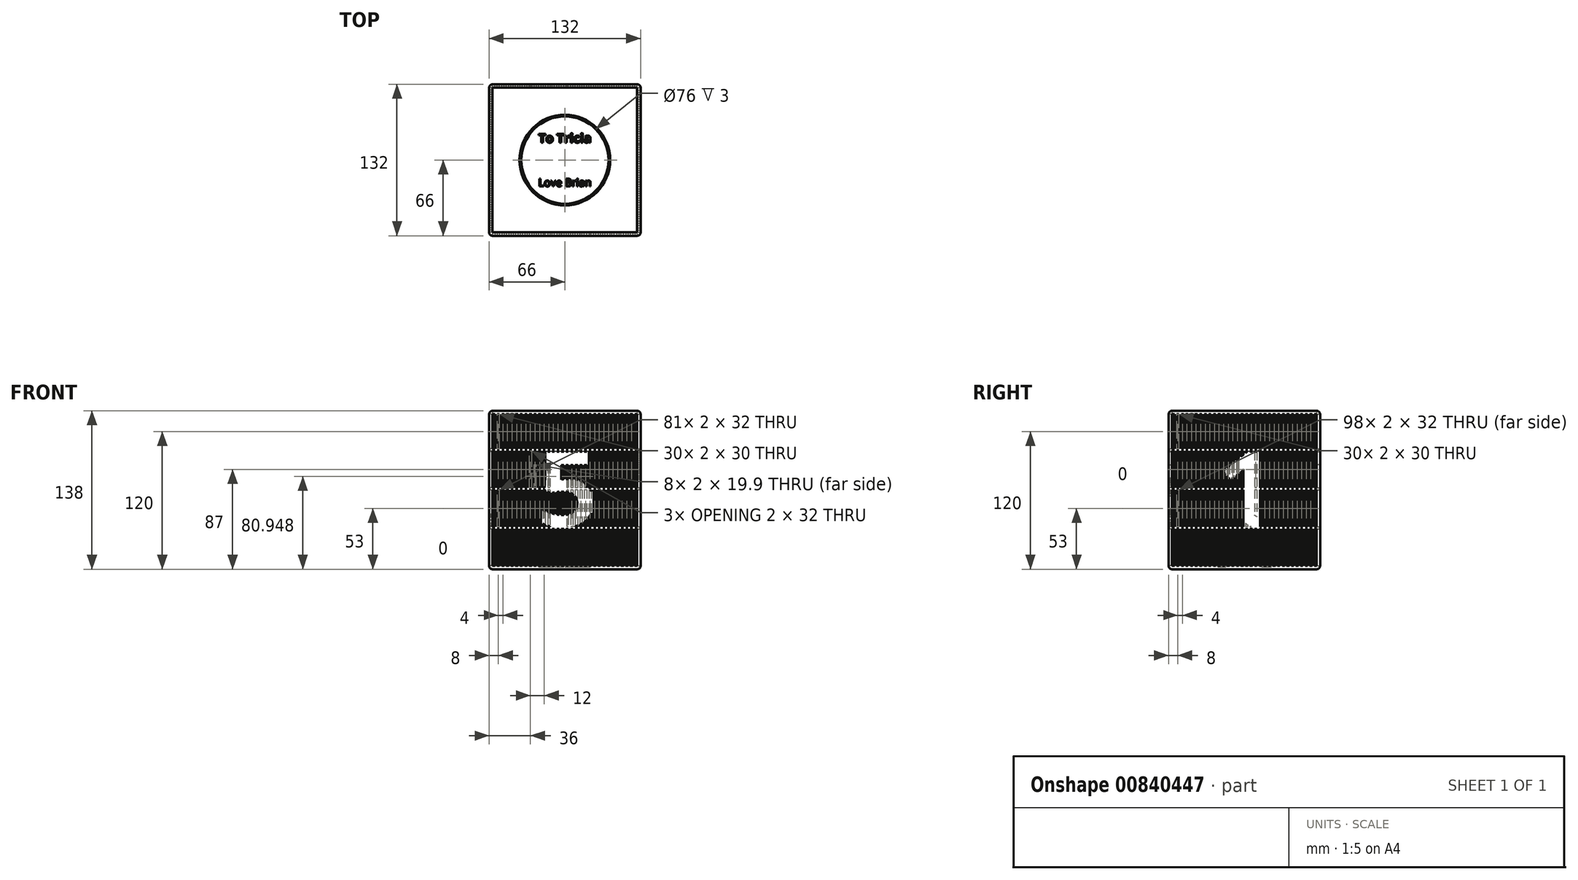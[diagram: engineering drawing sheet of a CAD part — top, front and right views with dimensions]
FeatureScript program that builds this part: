
annotation { "Feature Type Name" : "Feature", "Feature Type Description" : "" }
export const myFeature = defineFeature(function(context is Context, id is Id, definition is map)
    precondition{}
    {
        {
            var Q0;
            Q0=qCreatedBy(makeId("Top.planeOp"),FACE);
            var sketch = newSketch(context, id + "F0", { "sketchPlane" : qUnion([Q0])});
            skLineSegment(sketch, "E0.bottom", {"start": v(-66, 66) * mm, "end": v(66, 66) * mm});
            skLineSegment(sketch, "E0.top", {"start": v(-66, -66) * mm, "end": v(66, -66) * mm});
            skLineSegment(sketch, "E0.left", {"start": v(-66, 66) * mm, "end": v(-66, -66) * mm});
            skLineSegment(sketch, "E0.right", {"start": v(66, 66) * mm, "end": v(66, -66) * mm});
            skPoint(sketch, "E0.middle", {"position": v(0, 0) * mm});
            skSolve(sketch);
        }
        {
            var Q0;
            Q0 = qSketchRegion(id + "F0", true);
            extrude(context, id + "F1", {"entities" : qUnion([Q0]), "depth" : 3 * mm, "offsetDistance" : 25 * mm});
        }
        {
            var Q0;
            Q0=makeQuery(id+"F1.opExtrude","CAP_FACE",FACE,{"disambiguationData":[OSD([sQuery(id+"F0.wireOp",EDGE,"E0.bottom"),sQuery(id+"F0.wireOp",EDGE,"E0.top"),sQuery(id+"F0.wireOp",EDGE,"E0.left"),sQuery(id+"F0.wireOp",EDGE,"E0.right")])],"isStart":false});
            var sketch = newSketch(context, id + "F2", { "sketchPlane" : qUnion([Q0])});
            skCircle(sketch, "E1", {"center": v(0, 0) * mm, "radius": 38 * mm});
            skCircle(sketch, "E2", {"center": v(0, 0) * mm, "radius": 39.5 * mm});
            skSolve(sketch);
        }
        {
            var Q0;
            Q0 = qSketchRegion(id + "F2", true);
            extrude(context, id + "F3", {"entities" : qUnion([Q0]), "operationType" : NewBodyOperationType.ADD, "depth" : 3 * mm, "offsetDistance" : 25 * mm});
        }
        {
            var Q0;
            {var subQ0=sQuery(id+"F0.wireOp",EDGE,"E0.left");var subQ1=sQuery(id+"F0.wireOp",EDGE,"E0.top");var subQ2=sQuery(id+"F0.wireOp",EDGE,"E0.right");var subQ3=sQuery(id+"F0.wireOp",EDGE,"E0.bottom");Q0=makeQuery(id+"F3.boolean.opBoolean","SPLIT",FACE,{"disambiguationData":[TD([makeQuery(id+"F1.opExtrude","SWEPT_FACE",FACE,{"disambiguationData":[OSD([subQ3])]})])],"derivedFrom":makeQuery(id+"F1.opExtrude","CAP_FACE",FACE,{"disambiguationData":[OSD([subQ3,subQ1,subQ0,subQ2])],"isStart":false})});}
            var sketch = newSketch(context, id + "F4", { "sketchPlane" : qUnion([Q0])});
            skLineSegment(sketch, "E3.bottom", {"start": v(-66, 66) * mm, "end": v(66, 66) * mm});
            skLineSegment(sketch, "E3.top", {"start": v(-66, -66) * mm, "end": v(66, -66) * mm});
            skLineSegment(sketch, "E3.left", {"start": v(-66, 66) * mm, "end": v(-66, -66) * mm});
            skLineSegment(sketch, "E3.right", {"start": v(66, 66) * mm, "end": v(66, -66) * mm});
            skPoint(sketch, "E3.middle", {"position": v(0, 0) * mm});
            skLineSegment(sketch, "E4.bottom", {"start": v(-63, 63) * mm, "end": v(63, 63) * mm});
            skLineSegment(sketch, "E4.top", {"start": v(-63, -63) * mm, "end": v(63, -63) * mm});
            skLineSegment(sketch, "E4.left", {"start": v(-63, 63) * mm, "end": v(-63, -63) * mm});
            skLineSegment(sketch, "E4.right", {"start": v(63, 63) * mm, "end": v(63, -63) * mm});
            skSolve(sketch);
        }
        {
            var Q0;
            Q0 = qSketchRegion(id + "F4", true);
            extrude(context, id + "F5", {"entities" : qUnion([Q0]), "operationType" : NewBodyOperationType.ADD, "depth" : 135 * mm, "offsetDistance" : 25 * mm});
        }
        {
            var Q0;
            Q0=makeQuery(id+"F5.opExtrude","CAP_EDGE",EDGE,{"disambiguationData":[OSD([sQuery(id+"F4.wireOp",EDGE,"E3.bottom")])],"isStart":false});
            var Q1;
            Q1=makeQuery(id+"F5.opExtrude","CAP_EDGE",EDGE,{"disambiguationData":[OSD([sQuery(id+"F4.wireOp",EDGE,"E3.left")])],"isStart":false});
            var Q2;
            Q2=makeQuery(id+"F5.opExtrude","CAP_EDGE",EDGE,{"disambiguationData":[OSD([sQuery(id+"F4.wireOp",EDGE,"E3.top")])],"isStart":false});
            var Q3;
            Q3=makeQuery(id+"F5.opExtrude","CAP_EDGE",EDGE,{"disambiguationData":[OSD([sQuery(id+"F4.wireOp",EDGE,"E3.right")])],"isStart":false});
            var Q4;
            Q4=makeQuery(id+"F5.boolean.opBoolean","MERGE",EDGE,{"derivedFrom":[makeQuery(id+"F1.opExtrude","SWEPT_EDGE",EDGE,{"disambiguationData":[OSD([sQuery(id+"F0.wireOp",EDGE,"E0.top"),sQuery(id+"F0.wireOp",EDGE,"E0.right")])]}),makeQuery(id+"F5.opExtrude","SWEPT_EDGE",EDGE,{"disambiguationData":[OSD([sQuery(id+"F4.wireOp",EDGE,"E3.top"),sQuery(id+"F4.wireOp",EDGE,"E3.right")])]})]});
            var Q5;
            Q5=makeQuery(id+"F5.boolean.opBoolean","MERGE",EDGE,{"derivedFrom":[makeQuery(id+"F1.opExtrude","SWEPT_EDGE",EDGE,{"disambiguationData":[OSD([sQuery(id+"F0.wireOp",EDGE,"E0.top"),sQuery(id+"F0.wireOp",EDGE,"E0.left")])]}),makeQuery(id+"F5.opExtrude","SWEPT_EDGE",EDGE,{"disambiguationData":[OSD([sQuery(id+"F4.wireOp",EDGE,"E3.top"),sQuery(id+"F4.wireOp",EDGE,"E3.left")])]})]});
            var Q6;
            Q6=makeQuery(id+"F5.boolean.opBoolean","MERGE",EDGE,{"derivedFrom":[makeQuery(id+"F1.opExtrude","SWEPT_EDGE",EDGE,{"disambiguationData":[OSD([sQuery(id+"F0.wireOp",EDGE,"E0.bottom"),sQuery(id+"F0.wireOp",EDGE,"E0.left")])]}),makeQuery(id+"F5.opExtrude","SWEPT_EDGE",EDGE,{"disambiguationData":[OSD([sQuery(id+"F4.wireOp",EDGE,"E3.bottom"),sQuery(id+"F4.wireOp",EDGE,"E3.left")])]})]});
            var Q7;
            Q7=makeQuery(id+"F5.boolean.opBoolean","MERGE",EDGE,{"derivedFrom":[makeQuery(id+"F1.opExtrude","SWEPT_EDGE",EDGE,{"disambiguationData":[OSD([sQuery(id+"F0.wireOp",EDGE,"E0.bottom"),sQuery(id+"F0.wireOp",EDGE,"E0.right")])]}),makeQuery(id+"F5.opExtrude","SWEPT_EDGE",EDGE,{"disambiguationData":[OSD([sQuery(id+"F4.wireOp",EDGE,"E3.bottom"),sQuery(id+"F4.wireOp",EDGE,"E3.right")])]})]});
            var Q8;
            Q8=makeQuery(id+"F1.opExtrude","CAP_EDGE",EDGE,{"disambiguationData":[OSD([sQuery(id+"F0.wireOp",EDGE,"E0.bottom")])],"isStart":true});
            var Q9;
            Q9=makeQuery(id+"F1.opExtrude","CAP_EDGE",EDGE,{"disambiguationData":[OSD([sQuery(id+"F0.wireOp",EDGE,"E0.right")])],"isStart":true});
            var Q10;
            Q10=makeQuery(id+"F1.opExtrude","CAP_EDGE",EDGE,{"disambiguationData":[OSD([sQuery(id+"F0.wireOp",EDGE,"E0.left")])],"isStart":true});
            var Q11;
            Q11=makeQuery(id+"F1.opExtrude","CAP_EDGE",EDGE,{"disambiguationData":[OSD([sQuery(id+"F0.wireOp",EDGE,"E0.top")])],"isStart":true});
            fillet(context, id + "F6", {"entities" : qUnion([Q0, Q1, Q2, Q3, Q4, Q5, Q6, Q7, Q8, Q9, Q10, Q11]), "radius" : 3 * mm, "tangentPropagation" : true, "allowEdgeOverflow" : false});
        }
        {
            var Q0;
            Q0=makeQuery(id+"F5.boolean.opBoolean","MERGE",FACE,{"derivedFrom":[makeQuery(id+"F1.opExtrude","SWEPT_FACE",FACE,{"disambiguationData":[OSD([sQuery(id+"F0.wireOp",EDGE,"E0.top")])]}),makeQuery(id+"F5.opExtrude","SWEPT_FACE",FACE,{"disambiguationData":[OSD([sQuery(id+"F4.wireOp",EDGE,"E3.top")])]})]});
            var sketch = newSketch(context, id + "F7", { "sketchPlane" : qUnion([Q0])});
            skLineSegment(sketch, "E5.bottom", {"start": v(-63, 135) * mm, "end": v(-61, 135) * mm});
            skLineSegment(sketch, "E5.top", {"start": v(-63, 3) * mm, "end": v(-61, 3) * mm});
            skLineSegment(sketch, "E5.left", {"start": v(-63, 135) * mm, "end": v(-63, 3) * mm});
            skLineSegment(sketch, "E5.right", {"start": v(-61, 135) * mm, "end": v(-61, 3) * mm});
            skLineSegment(sketch, "E6.bottom", {"start": v(-59, 135) * mm, "end": v(-57, 135) * mm});
            skLineSegment(sketch, "E6.top", {"start": v(-59, 3) * mm, "end": v(-57, 3) * mm});
            skLineSegment(sketch, "E6.left", {"start": v(-59, 135) * mm, "end": v(-59, 3) * mm});
            skLineSegment(sketch, "E6.right", {"start": v(-57, 135) * mm, "end": v(-57, 3) * mm});
            skLineSegment(sketch, "E7.bottom", {"start": v(-55, 135) * mm, "end": v(-53, 135) * mm});
            skLineSegment(sketch, "E7.top", {"start": v(-55, 3) * mm, "end": v(-53, 3) * mm});
            skLineSegment(sketch, "E7.left", {"start": v(-55, 135) * mm, "end": v(-55, 3) * mm});
            skLineSegment(sketch, "E7.right", {"start": v(-53, 135) * mm, "end": v(-53, 3) * mm});
            skLineSegment(sketch, "E8.bottom", {"start": v(-51, 135) * mm, "end": v(-49, 135) * mm});
            skLineSegment(sketch, "E8.top", {"start": v(-51, 3) * mm, "end": v(-49, 3) * mm});
            skLineSegment(sketch, "E8.left", {"start": v(-51, 135) * mm, "end": v(-51, 3) * mm});
            skLineSegment(sketch, "E8.right", {"start": v(-49, 135) * mm, "end": v(-49, 3) * mm});
            skLineSegment(sketch, "E9.bottom", {"start": v(-47, 135) * mm, "end": v(-45, 135) * mm});
            skLineSegment(sketch, "E9.top", {"start": v(-47, 3) * mm, "end": v(-45, 3) * mm});
            skLineSegment(sketch, "E9.left", {"start": v(-47, 135) * mm, "end": v(-47, 3) * mm});
            skLineSegment(sketch, "E9.right", {"start": v(-45, 135) * mm, "end": v(-45, 3) * mm});
            skLineSegment(sketch, "E10.bottom", {"start": v(-43, 135) * mm, "end": v(-41, 135) * mm});
            skLineSegment(sketch, "E10.top", {"start": v(-43, 3) * mm, "end": v(-41, 3) * mm});
            skLineSegment(sketch, "E10.left", {"start": v(-43, 135) * mm, "end": v(-43, 3) * mm});
            skLineSegment(sketch, "E10.right", {"start": v(-41, 135) * mm, "end": v(-41, 3) * mm});
            skLineSegment(sketch, "E11.bottom", {"start": v(-39, 135) * mm, "end": v(-37, 135) * mm});
            skLineSegment(sketch, "E11.top", {"start": v(-39, 3) * mm, "end": v(-37, 3) * mm});
            skLineSegment(sketch, "E11.left", {"start": v(-39, 135) * mm, "end": v(-39, 3) * mm});
            skLineSegment(sketch, "E11.right", {"start": v(-37, 135) * mm, "end": v(-37, 3) * mm});
            skLineSegment(sketch, "E12.bottom", {"start": v(-35, 135) * mm, "end": v(-33, 135) * mm});
            skLineSegment(sketch, "E12.top", {"start": v(-35, 3) * mm, "end": v(-33, 3) * mm});
            skLineSegment(sketch, "E12.left", {"start": v(-35, 135) * mm, "end": v(-35, 3) * mm});
            skLineSegment(sketch, "E12.right", {"start": v(-33, 135) * mm, "end": v(-33, 3) * mm});
            skLineSegment(sketch, "E13.bottom", {"start": v(-31, 135) * mm, "end": v(-29, 135) * mm});
            skLineSegment(sketch, "E13.top", {"start": v(-31, 3) * mm, "end": v(-29, 3) * mm});
            skLineSegment(sketch, "E13.left", {"start": v(-31, 135) * mm, "end": v(-31, 3) * mm});
            skLineSegment(sketch, "E13.right", {"start": v(-29, 135) * mm, "end": v(-29, 3) * mm});
            skLineSegment(sketch, "E14.bottom", {"start": v(-27, 135) * mm, "end": v(-25, 135) * mm});
            skLineSegment(sketch, "E14.top", {"start": v(-27, 3) * mm, "end": v(-25, 3) * mm});
            skLineSegment(sketch, "E14.left", {"start": v(-27, 135) * mm, "end": v(-27, 3) * mm});
            skLineSegment(sketch, "E14.right", {"start": v(-25, 135) * mm, "end": v(-25, 3) * mm});
            skLineSegment(sketch, "E15.bottom", {"start": v(-23, 135) * mm, "end": v(-21, 135) * mm});
            skLineSegment(sketch, "E15.top", {"start": v(-23, 3) * mm, "end": v(-21, 3) * mm});
            skLineSegment(sketch, "E15.left", {"start": v(-23, 135) * mm, "end": v(-23, 3) * mm});
            skLineSegment(sketch, "E15.right", {"start": v(-21, 135) * mm, "end": v(-21, 3) * mm});
            skLineSegment(sketch, "E16.bottom", {"start": v(-19, 3) * mm, "end": v(-17, 3) * mm});
            skLineSegment(sketch, "E16.top", {"start": v(-19, 135) * mm, "end": v(-17, 135) * mm});
            skLineSegment(sketch, "E16.left", {"start": v(-19, 3) * mm, "end": v(-19, 135) * mm});
            skLineSegment(sketch, "E16.right", {"start": v(-17, 3) * mm, "end": v(-17, 135) * mm});
            skLineSegment(sketch, "E17.bottom", {"start": v(-15, 135) * mm, "end": v(-13, 135) * mm});
            skLineSegment(sketch, "E17.top", {"start": v(-15, 3) * mm, "end": v(-13, 3) * mm});
            skLineSegment(sketch, "E17.left", {"start": v(-15, 135) * mm, "end": v(-15, 3) * mm});
            skLineSegment(sketch, "E17.right", {"start": v(-13, 135) * mm, "end": v(-13, 3) * mm});
            skLineSegment(sketch, "E18.bottom", {"start": v(-11, 3) * mm, "end": v(-9, 3) * mm});
            skLineSegment(sketch, "E18.top", {"start": v(-11, 135) * mm, "end": v(-9, 135) * mm});
            skLineSegment(sketch, "E18.left", {"start": v(-11, 3) * mm, "end": v(-11, 135) * mm});
            skLineSegment(sketch, "E18.right", {"start": v(-9, 3) * mm, "end": v(-9, 135) * mm});
            skLineSegment(sketch, "E19.bottom", {"start": v(-7, 135) * mm, "end": v(-5, 135) * mm});
            skLineSegment(sketch, "E19.top", {"start": v(-7, 3) * mm, "end": v(-5, 3) * mm});
            skLineSegment(sketch, "E19.left", {"start": v(-7, 135) * mm, "end": v(-7, 3) * mm});
            skLineSegment(sketch, "E19.right", {"start": v(-5, 135) * mm, "end": v(-5, 3) * mm});
            skLineSegment(sketch, "E20.bottom", {"start": v(-3, 3) * mm, "end": v(-1, 3) * mm});
            skLineSegment(sketch, "E20.top", {"start": v(-3, 135) * mm, "end": v(-1, 135) * mm});
            skLineSegment(sketch, "E20.left", {"start": v(-3, 3) * mm, "end": v(-3, 135) * mm});
            skLineSegment(sketch, "E20.right", {"start": v(-1, 3) * mm, "end": v(-1, 135) * mm});
            skLineSegment(sketch, "E21.bottom", {"start": v(1, 135) * mm, "end": v(3, 135) * mm});
            skLineSegment(sketch, "E21.top", {"start": v(1, 3) * mm, "end": v(3, 3) * mm});
            skLineSegment(sketch, "E21.left", {"start": v(1, 135) * mm, "end": v(1, 3) * mm});
            skLineSegment(sketch, "E21.right", {"start": v(3, 135) * mm, "end": v(3, 3) * mm});
            skLineSegment(sketch, "E22.bottom", {"start": v(5, 3) * mm, "end": v(7, 3) * mm});
            skLineSegment(sketch, "E22.top", {"start": v(5, 135) * mm, "end": v(7, 135) * mm});
            skLineSegment(sketch, "E22.left", {"start": v(5, 3) * mm, "end": v(5, 135) * mm});
            skLineSegment(sketch, "E22.right", {"start": v(7, 3) * mm, "end": v(7, 135) * mm});
            skLineSegment(sketch, "E23.bottom", {"start": v(9, 135) * mm, "end": v(11, 135) * mm});
            skLineSegment(sketch, "E23.top", {"start": v(9, 3) * mm, "end": v(11, 3) * mm});
            skLineSegment(sketch, "E23.left", {"start": v(9, 135) * mm, "end": v(9, 3) * mm});
            skLineSegment(sketch, "E23.right", {"start": v(11, 135) * mm, "end": v(11, 3) * mm});
            skLineSegment(sketch, "E24.bottom", {"start": v(13, 3) * mm, "end": v(15, 3) * mm});
            skLineSegment(sketch, "E24.top", {"start": v(13, 135) * mm, "end": v(15, 135) * mm});
            skLineSegment(sketch, "E24.left", {"start": v(13, 3) * mm, "end": v(13, 135) * mm});
            skLineSegment(sketch, "E24.right", {"start": v(15, 3) * mm, "end": v(15, 135) * mm});
            skLineSegment(sketch, "E25.bottom", {"start": v(17, 135) * mm, "end": v(19, 135) * mm});
            skLineSegment(sketch, "E25.top", {"start": v(17, 3) * mm, "end": v(19, 3) * mm});
            skLineSegment(sketch, "E25.left", {"start": v(17, 135) * mm, "end": v(17, 3) * mm});
            skLineSegment(sketch, "E25.right", {"start": v(19, 135) * mm, "end": v(19, 3) * mm});
            skLineSegment(sketch, "E26.bottom", {"start": v(21, 135) * mm, "end": v(23, 135) * mm});
            skLineSegment(sketch, "E26.top", {"start": v(21, 3) * mm, "end": v(23, 3) * mm});
            skLineSegment(sketch, "E26.left", {"start": v(21, 135) * mm, "end": v(21, 3) * mm});
            skLineSegment(sketch, "E26.right", {"start": v(23, 135) * mm, "end": v(23, 3) * mm});
            skLineSegment(sketch, "E27.bottom", {"start": v(25, 3) * mm, "end": v(27, 3) * mm});
            skLineSegment(sketch, "E27.top", {"start": v(25, 135) * mm, "end": v(27, 135) * mm});
            skLineSegment(sketch, "E27.left", {"start": v(25, 3) * mm, "end": v(25, 135) * mm});
            skLineSegment(sketch, "E27.right", {"start": v(27, 3) * mm, "end": v(27, 135) * mm});
            skLineSegment(sketch, "E28.bottom", {"start": v(29, 135) * mm, "end": v(31, 135) * mm});
            skLineSegment(sketch, "E28.top", {"start": v(29, 3) * mm, "end": v(31, 3) * mm});
            skLineSegment(sketch, "E28.left", {"start": v(29, 135) * mm, "end": v(29, 3) * mm});
            skLineSegment(sketch, "E28.right", {"start": v(31, 135) * mm, "end": v(31, 3) * mm});
            skLineSegment(sketch, "E29.bottom", {"start": v(33, 3) * mm, "end": v(35, 3) * mm});
            skLineSegment(sketch, "E29.top", {"start": v(33, 135) * mm, "end": v(35, 135) * mm});
            skLineSegment(sketch, "E29.left", {"start": v(33, 3) * mm, "end": v(33, 135) * mm});
            skLineSegment(sketch, "E29.right", {"start": v(35, 3) * mm, "end": v(35, 135) * mm});
            skLineSegment(sketch, "E30.bottom", {"start": v(37, 135) * mm, "end": v(39, 135) * mm});
            skLineSegment(sketch, "E30.top", {"start": v(37, 3) * mm, "end": v(39, 3) * mm});
            skLineSegment(sketch, "E30.left", {"start": v(37, 135) * mm, "end": v(37, 3) * mm});
            skLineSegment(sketch, "E30.right", {"start": v(39, 135) * mm, "end": v(39, 3) * mm});
            skLineSegment(sketch, "E31.bottom", {"start": v(41, 3) * mm, "end": v(43, 3) * mm});
            skLineSegment(sketch, "E31.top", {"start": v(41, 135) * mm, "end": v(43, 135) * mm});
            skLineSegment(sketch, "E31.left", {"start": v(41, 3) * mm, "end": v(41, 135) * mm});
            skLineSegment(sketch, "E31.right", {"start": v(43, 3) * mm, "end": v(43, 135) * mm});
            skLineSegment(sketch, "E32.bottom", {"start": v(45, 135) * mm, "end": v(47, 135) * mm});
            skLineSegment(sketch, "E32.top", {"start": v(45, 3) * mm, "end": v(47, 3) * mm});
            skLineSegment(sketch, "E32.left", {"start": v(45, 135) * mm, "end": v(45, 3) * mm});
            skLineSegment(sketch, "E32.right", {"start": v(47, 135) * mm, "end": v(47, 3) * mm});
            skLineSegment(sketch, "E33.bottom", {"start": v(49, 3) * mm, "end": v(51, 3) * mm});
            skLineSegment(sketch, "E33.top", {"start": v(49, 135) * mm, "end": v(51, 135) * mm});
            skLineSegment(sketch, "E33.left", {"start": v(49, 3) * mm, "end": v(49, 135) * mm});
            skLineSegment(sketch, "E33.right", {"start": v(51, 3) * mm, "end": v(51, 135) * mm});
            skLineSegment(sketch, "E34.bottom", {"start": v(53, 135) * mm, "end": v(55, 135) * mm});
            skLineSegment(sketch, "E34.top", {"start": v(53, 3) * mm, "end": v(55, 3) * mm});
            skLineSegment(sketch, "E34.left", {"start": v(53, 135) * mm, "end": v(53, 3) * mm});
            skLineSegment(sketch, "E34.right", {"start": v(55, 135) * mm, "end": v(55, 3) * mm});
            skLineSegment(sketch, "E35.bottom", {"start": v(57, 135) * mm, "end": v(59, 135) * mm});
            skLineSegment(sketch, "E35.top", {"start": v(57, 3) * mm, "end": v(59, 3) * mm});
            skLineSegment(sketch, "E35.left", {"start": v(57, 135) * mm, "end": v(57, 3) * mm});
            skLineSegment(sketch, "E35.right", {"start": v(59, 135) * mm, "end": v(59, 3) * mm});
            skLineSegment(sketch, "E36.bottom", {"start": v(61, 135) * mm, "end": v(63, 135) * mm});
            skLineSegment(sketch, "E36.top", {"start": v(61, 3) * mm, "end": v(63, 3) * mm});
            skLineSegment(sketch, "E36.left", {"start": v(61, 135) * mm, "end": v(61, 3) * mm});
            skLineSegment(sketch, "E36.right", {"start": v(63, 135) * mm, "end": v(63, 3) * mm});
            skSolve(sketch);
        }
        {
            var Q0;
            Q0 = qSketchRegion(id + "F7", true);
            extrude(context, id + "F8", {"entities" : qUnion([Q0]), "operationType" : NewBodyOperationType.REMOVE, "oppositeDirection" : true, "depth" : 3 * mm, "offsetDistance" : 25 * mm});
        }
        {
            var Q0;
            Q0=makeQuery(id+"F5.boolean.opBoolean","MERGE",FACE,{"derivedFrom":[makeQuery(id+"F1.opExtrude","SWEPT_FACE",FACE,{"disambiguationData":[OSD([sQuery(id+"F0.wireOp",EDGE,"E0.right")])]}),makeQuery(id+"F5.opExtrude","SWEPT_FACE",FACE,{"disambiguationData":[OSD([sQuery(id+"F4.wireOp",EDGE,"E3.right")])]})]});
            var sketch = newSketch(context, id + "F9", { "sketchPlane" : qUnion([Q0])});
            skLineSegment(sketch, "E37.bottom", {"start": v(-63, 135) * mm, "end": v(-61, 135) * mm});
            skLineSegment(sketch, "E37.top", {"start": v(-63, 3) * mm, "end": v(-61, 3) * mm});
            skLineSegment(sketch, "E37.left", {"start": v(-63, 135) * mm, "end": v(-63, 3) * mm});
            skLineSegment(sketch, "E37.right", {"start": v(-61, 135) * mm, "end": v(-61, 3) * mm});
            skLineSegment(sketch, "E38.bottom", {"start": v(-59, 135) * mm, "end": v(-57, 135) * mm});
            skLineSegment(sketch, "E38.top", {"start": v(-59, 3) * mm, "end": v(-57, 3) * mm});
            skLineSegment(sketch, "E38.left", {"start": v(-59, 135) * mm, "end": v(-59, 3) * mm});
            skLineSegment(sketch, "E38.right", {"start": v(-57, 135) * mm, "end": v(-57, 3) * mm});
            skLineSegment(sketch, "E39.bottom", {"start": v(-55, 135) * mm, "end": v(-53, 135) * mm});
            skLineSegment(sketch, "E39.top", {"start": v(-55, 3) * mm, "end": v(-53, 3) * mm});
            skLineSegment(sketch, "E39.left", {"start": v(-55, 135) * mm, "end": v(-55, 3) * mm});
            skLineSegment(sketch, "E39.right", {"start": v(-53, 135) * mm, "end": v(-53, 3) * mm});
            skLineSegment(sketch, "E40.bottom", {"start": v(-51, 135) * mm, "end": v(-49, 135) * mm});
            skLineSegment(sketch, "E40.top", {"start": v(-51, 3) * mm, "end": v(-49, 3) * mm});
            skLineSegment(sketch, "E40.left", {"start": v(-51, 135) * mm, "end": v(-51, 3) * mm});
            skLineSegment(sketch, "E40.right", {"start": v(-49, 135) * mm, "end": v(-49, 3) * mm});
            skLineSegment(sketch, "E41.bottom", {"start": v(-47, 135) * mm, "end": v(-45, 135) * mm});
            skLineSegment(sketch, "E41.top", {"start": v(-47, 3) * mm, "end": v(-45, 3) * mm});
            skLineSegment(sketch, "E41.left", {"start": v(-47, 135) * mm, "end": v(-47, 3) * mm});
            skLineSegment(sketch, "E41.right", {"start": v(-45, 135) * mm, "end": v(-45, 3) * mm});
            skLineSegment(sketch, "E42.bottom", {"start": v(-43, 135) * mm, "end": v(-41, 135) * mm});
            skLineSegment(sketch, "E42.top", {"start": v(-43, 3) * mm, "end": v(-41, 3) * mm});
            skLineSegment(sketch, "E42.left", {"start": v(-43, 135) * mm, "end": v(-43, 3) * mm});
            skLineSegment(sketch, "E42.right", {"start": v(-41, 135) * mm, "end": v(-41, 3) * mm});
            skLineSegment(sketch, "E43.bottom", {"start": v(-39, 135) * mm, "end": v(-37, 135) * mm});
            skLineSegment(sketch, "E43.top", {"start": v(-39, 3) * mm, "end": v(-37, 3) * mm});
            skLineSegment(sketch, "E43.left", {"start": v(-39, 135) * mm, "end": v(-39, 3) * mm});
            skLineSegment(sketch, "E43.right", {"start": v(-37, 135) * mm, "end": v(-37, 3) * mm});
            skLineSegment(sketch, "E44.bottom", {"start": v(-35, 135) * mm, "end": v(-33, 135) * mm});
            skLineSegment(sketch, "E44.top", {"start": v(-35, 3) * mm, "end": v(-33, 3) * mm});
            skLineSegment(sketch, "E44.left", {"start": v(-35, 135) * mm, "end": v(-35, 3) * mm});
            skLineSegment(sketch, "E44.right", {"start": v(-33, 135) * mm, "end": v(-33, 3) * mm});
            skLineSegment(sketch, "E45.bottom", {"start": v(-31, 135) * mm, "end": v(-29, 135) * mm});
            skLineSegment(sketch, "E45.top", {"start": v(-31, 3) * mm, "end": v(-29, 3) * mm});
            skLineSegment(sketch, "E45.left", {"start": v(-31, 135) * mm, "end": v(-31, 3) * mm});
            skLineSegment(sketch, "E45.right", {"start": v(-29, 135) * mm, "end": v(-29, 3) * mm});
            skLineSegment(sketch, "E46.bottom", {"start": v(-27, 135) * mm, "end": v(-25, 135) * mm});
            skLineSegment(sketch, "E46.top", {"start": v(-27, 3) * mm, "end": v(-25, 3) * mm});
            skLineSegment(sketch, "E46.left", {"start": v(-27, 135) * mm, "end": v(-27, 3) * mm});
            skLineSegment(sketch, "E46.right", {"start": v(-25, 135) * mm, "end": v(-25, 3) * mm});
            skLineSegment(sketch, "E47.bottom", {"start": v(-23, 135) * mm, "end": v(-21, 135) * mm});
            skLineSegment(sketch, "E47.top", {"start": v(-23, 3) * mm, "end": v(-21, 3) * mm});
            skLineSegment(sketch, "E47.left", {"start": v(-23, 135) * mm, "end": v(-23, 3) * mm});
            skLineSegment(sketch, "E47.right", {"start": v(-21, 135) * mm, "end": v(-21, 3) * mm});
            skLineSegment(sketch, "E48.bottom", {"start": v(-19, 135) * mm, "end": v(-17, 135) * mm});
            skLineSegment(sketch, "E48.top", {"start": v(-19, 3) * mm, "end": v(-17, 3) * mm});
            skLineSegment(sketch, "E48.left", {"start": v(-19, 135) * mm, "end": v(-19, 3) * mm});
            skLineSegment(sketch, "E48.right", {"start": v(-17, 135) * mm, "end": v(-17, 3) * mm});
            skPoint(sketch, "E49.oppositeSnap0", {"position": v(0, 135) * mm});
            skLineSegment(sketch, "E50.bottom", {"start": v(-15, 135) * mm, "end": v(-13, 135) * mm});
            skLineSegment(sketch, "E50.top", {"start": v(-15, 3) * mm, "end": v(-13, 3) * mm});
            skLineSegment(sketch, "E50.left", {"start": v(-15, 135) * mm, "end": v(-15, 3) * mm});
            skLineSegment(sketch, "E50.right", {"start": v(-13, 135) * mm, "end": v(-13, 3) * mm});
            skLineSegment(sketch, "E51.bottom", {"start": v(-11, 135) * mm, "end": v(-9, 135) * mm});
            skLineSegment(sketch, "E51.top", {"start": v(-11, 3) * mm, "end": v(-9, 3) * mm});
            skLineSegment(sketch, "E51.left", {"start": v(-11, 135) * mm, "end": v(-11, 3) * mm});
            skLineSegment(sketch, "E51.right", {"start": v(-9, 135) * mm, "end": v(-9, 3) * mm});
            skLineSegment(sketch, "E52.bottom", {"start": v(-7, 135) * mm, "end": v(-5, 135) * mm});
            skLineSegment(sketch, "E52.top", {"start": v(-7, 3) * mm, "end": v(-5, 3) * mm});
            skLineSegment(sketch, "E52.left", {"start": v(-7, 135) * mm, "end": v(-7, 3) * mm});
            skLineSegment(sketch, "E52.right", {"start": v(-5, 135) * mm, "end": v(-5, 3) * mm});
            skLineSegment(sketch, "E53.bottom", {"start": v(-3, 135) * mm, "end": v(-1, 135) * mm});
            skLineSegment(sketch, "E53.top", {"start": v(-3, 3) * mm, "end": v(-1, 3) * mm});
            skLineSegment(sketch, "E53.left", {"start": v(-3, 135) * mm, "end": v(-3, 3) * mm});
            skLineSegment(sketch, "E53.right", {"start": v(-1, 135) * mm, "end": v(-1, 3) * mm});
            skLineSegment(sketch, "E54.bottom", {"start": v(1, 135) * mm, "end": v(3, 135) * mm});
            skLineSegment(sketch, "E54.top", {"start": v(1, 3) * mm, "end": v(3, 3) * mm});
            skLineSegment(sketch, "E54.left", {"start": v(1, 135) * mm, "end": v(1, 3) * mm});
            skLineSegment(sketch, "E54.right", {"start": v(3, 135) * mm, "end": v(3, 3) * mm});
            skLineSegment(sketch, "E55.bottom", {"start": v(5, 135) * mm, "end": v(7, 135) * mm});
            skLineSegment(sketch, "E55.top", {"start": v(5, 3) * mm, "end": v(7, 3) * mm});
            skLineSegment(sketch, "E55.left", {"start": v(5, 135) * mm, "end": v(5, 3) * mm});
            skLineSegment(sketch, "E55.right", {"start": v(7, 135) * mm, "end": v(7, 3) * mm});
            skLineSegment(sketch, "E56.bottom", {"start": v(9, 135) * mm, "end": v(11, 135) * mm});
            skLineSegment(sketch, "E56.top", {"start": v(9, 3) * mm, "end": v(11, 3) * mm});
            skLineSegment(sketch, "E56.left", {"start": v(9, 135) * mm, "end": v(9, 3) * mm});
            skLineSegment(sketch, "E56.right", {"start": v(11, 135) * mm, "end": v(11, 3) * mm});
            skLineSegment(sketch, "E57.bottom", {"start": v(13, 135) * mm, "end": v(15, 135) * mm});
            skLineSegment(sketch, "E57.top", {"start": v(13, 3) * mm, "end": v(15, 3) * mm});
            skLineSegment(sketch, "E57.left", {"start": v(13, 135) * mm, "end": v(13, 3) * mm});
            skLineSegment(sketch, "E57.right", {"start": v(15, 135) * mm, "end": v(15, 3) * mm});
            skLineSegment(sketch, "E58.bottom", {"start": v(17, 135) * mm, "end": v(19, 135) * mm});
            skLineSegment(sketch, "E58.top", {"start": v(17, 3) * mm, "end": v(19, 3) * mm});
            skLineSegment(sketch, "E58.left", {"start": v(17, 135) * mm, "end": v(17, 3) * mm});
            skLineSegment(sketch, "E58.right", {"start": v(19, 135) * mm, "end": v(19, 3) * mm});
            skLineSegment(sketch, "E59.bottom", {"start": v(21, 135) * mm, "end": v(23, 135) * mm});
            skLineSegment(sketch, "E59.top", {"start": v(21, 3) * mm, "end": v(23, 3) * mm});
            skLineSegment(sketch, "E59.left", {"start": v(21, 135) * mm, "end": v(21, 3) * mm});
            skLineSegment(sketch, "E59.right", {"start": v(23, 135) * mm, "end": v(23, 3) * mm});
            skLineSegment(sketch, "E60.bottom", {"start": v(25, 135) * mm, "end": v(27, 135) * mm});
            skLineSegment(sketch, "E60.top", {"start": v(25, 3) * mm, "end": v(27, 3) * mm});
            skLineSegment(sketch, "E60.left", {"start": v(25, 135) * mm, "end": v(25, 3) * mm});
            skLineSegment(sketch, "E60.right", {"start": v(27, 135) * mm, "end": v(27, 3) * mm});
            skLineSegment(sketch, "E61.bottom", {"start": v(29, 135) * mm, "end": v(31, 135) * mm});
            skLineSegment(sketch, "E61.top", {"start": v(29, 3) * mm, "end": v(31, 3) * mm});
            skLineSegment(sketch, "E61.left", {"start": v(29, 135) * mm, "end": v(29, 3) * mm});
            skLineSegment(sketch, "E61.right", {"start": v(31, 135) * mm, "end": v(31, 3) * mm});
            skLineSegment(sketch, "E62.bottom", {"start": v(33, 135) * mm, "end": v(35, 135) * mm});
            skLineSegment(sketch, "E62.top", {"start": v(33, 3) * mm, "end": v(35, 3) * mm});
            skLineSegment(sketch, "E62.left", {"start": v(33, 135) * mm, "end": v(33, 3) * mm});
            skLineSegment(sketch, "E62.right", {"start": v(35, 135) * mm, "end": v(35, 3) * mm});
            skLineSegment(sketch, "E63.bottom", {"start": v(37, 135) * mm, "end": v(39, 135) * mm});
            skLineSegment(sketch, "E63.top", {"start": v(37, 3) * mm, "end": v(39, 3) * mm});
            skLineSegment(sketch, "E63.left", {"start": v(37, 135) * mm, "end": v(37, 3) * mm});
            skLineSegment(sketch, "E63.right", {"start": v(39, 135) * mm, "end": v(39, 3) * mm});
            skLineSegment(sketch, "E64.bottom", {"start": v(41, 135) * mm, "end": v(43, 135) * mm});
            skLineSegment(sketch, "E64.top", {"start": v(41, 3) * mm, "end": v(43, 3) * mm});
            skLineSegment(sketch, "E64.left", {"start": v(41, 135) * mm, "end": v(41, 3) * mm});
            skLineSegment(sketch, "E64.right", {"start": v(43, 135) * mm, "end": v(43, 3) * mm});
            skLineSegment(sketch, "E65.bottom", {"start": v(45, 135) * mm, "end": v(47, 135) * mm});
            skLineSegment(sketch, "E65.top", {"start": v(45, 3) * mm, "end": v(47, 3) * mm});
            skLineSegment(sketch, "E65.left", {"start": v(45, 135) * mm, "end": v(45, 3) * mm});
            skLineSegment(sketch, "E65.right", {"start": v(47, 135) * mm, "end": v(47, 3) * mm});
            skLineSegment(sketch, "E66.bottom", {"start": v(49, 135) * mm, "end": v(51, 135) * mm});
            skLineSegment(sketch, "E66.top", {"start": v(49, 3) * mm, "end": v(51, 3) * mm});
            skLineSegment(sketch, "E66.left", {"start": v(49, 135) * mm, "end": v(49, 3) * mm});
            skLineSegment(sketch, "E66.right", {"start": v(51, 135) * mm, "end": v(51, 3) * mm});
            skLineSegment(sketch, "E67.bottom", {"start": v(53, 135) * mm, "end": v(55, 135) * mm});
            skLineSegment(sketch, "E67.top", {"start": v(53, 3) * mm, "end": v(55, 3) * mm});
            skLineSegment(sketch, "E67.left", {"start": v(53, 135) * mm, "end": v(53, 3) * mm});
            skLineSegment(sketch, "E67.right", {"start": v(55, 135) * mm, "end": v(55, 3) * mm});
            skLineSegment(sketch, "E68.bottom", {"start": v(57, 135) * mm, "end": v(59, 135) * mm});
            skLineSegment(sketch, "E68.top", {"start": v(57, 3) * mm, "end": v(59, 3) * mm});
            skLineSegment(sketch, "E68.left", {"start": v(57, 135) * mm, "end": v(57, 3) * mm});
            skLineSegment(sketch, "E68.right", {"start": v(59, 135) * mm, "end": v(59, 3) * mm});
            skLineSegment(sketch, "E69.bottom", {"start": v(61, 135) * mm, "end": v(63, 135) * mm});
            skLineSegment(sketch, "E69.top", {"start": v(61, 3) * mm, "end": v(63, 3) * mm});
            skLineSegment(sketch, "E69.left", {"start": v(61, 135) * mm, "end": v(61, 3) * mm});
            skLineSegment(sketch, "E69.right", {"start": v(63, 135) * mm, "end": v(63, 3) * mm});
            skSolve(sketch);
        }
        {
            var Q0;
            Q0 = qSketchRegion(id + "F9", true);
            extrude(context, id + "F10", {"entities" : qUnion([Q0]), "operationType" : NewBodyOperationType.REMOVE, "oppositeDirection" : true, "depth" : 3 * mm, "offsetDistance" : 25 * mm});
        }
        {
            var Q0;
            Q0=makeQuery(id+"F5.boolean.opBoolean","MERGE",FACE,{"derivedFrom":[makeQuery(id+"F1.opExtrude","SWEPT_FACE",FACE,{"disambiguationData":[OSD([sQuery(id+"F0.wireOp",EDGE,"E0.bottom")])]}),makeQuery(id+"F5.opExtrude","SWEPT_FACE",FACE,{"disambiguationData":[OSD([sQuery(id+"F4.wireOp",EDGE,"E3.bottom")])]})]});
            var sketch = newSketch(context, id + "F11", { "sketchPlane" : qUnion([Q0])});
            skLineSegment(sketch, "E70.bottom", {"start": v(-63, 135) * mm, "end": v(-61, 135) * mm});
            skLineSegment(sketch, "E70.top", {"start": v(-63, 3) * mm, "end": v(-61, 3) * mm});
            skLineSegment(sketch, "E70.left", {"start": v(-63, 135) * mm, "end": v(-63, 3) * mm});
            skLineSegment(sketch, "E70.right", {"start": v(-61, 135) * mm, "end": v(-61, 3) * mm});
            skLineSegment(sketch, "E71.bottom", {"start": v(-59, 135) * mm, "end": v(-57, 135) * mm});
            skLineSegment(sketch, "E71.top", {"start": v(-59, 3) * mm, "end": v(-57, 3) * mm});
            skLineSegment(sketch, "E71.left", {"start": v(-59, 135) * mm, "end": v(-59, 3) * mm});
            skLineSegment(sketch, "E71.right", {"start": v(-57, 135) * mm, "end": v(-57, 3) * mm});
            skLineSegment(sketch, "E72.bottom", {"start": v(-55, 135) * mm, "end": v(-53, 135) * mm});
            skLineSegment(sketch, "E72.top", {"start": v(-55, 3) * mm, "end": v(-53, 3) * mm});
            skLineSegment(sketch, "E72.left", {"start": v(-55, 135) * mm, "end": v(-55, 3) * mm});
            skLineSegment(sketch, "E72.right", {"start": v(-53, 135) * mm, "end": v(-53, 3) * mm});
            skLineSegment(sketch, "E73.bottom", {"start": v(-51, 135) * mm, "end": v(-49, 135) * mm});
            skLineSegment(sketch, "E73.top", {"start": v(-51, 3) * mm, "end": v(-49, 3) * mm});
            skLineSegment(sketch, "E73.left", {"start": v(-51, 135) * mm, "end": v(-51, 3) * mm});
            skLineSegment(sketch, "E73.right", {"start": v(-49, 135) * mm, "end": v(-49, 3) * mm});
            skLineSegment(sketch, "E74.bottom", {"start": v(-47, 135) * mm, "end": v(-45, 135) * mm});
            skLineSegment(sketch, "E74.top", {"start": v(-47, 3) * mm, "end": v(-45, 3) * mm});
            skLineSegment(sketch, "E74.left", {"start": v(-47, 135) * mm, "end": v(-47, 3) * mm});
            skLineSegment(sketch, "E74.right", {"start": v(-45, 135) * mm, "end": v(-45, 3) * mm});
            skLineSegment(sketch, "E75.bottom", {"start": v(-43, 135) * mm, "end": v(-41, 135) * mm});
            skLineSegment(sketch, "E75.top", {"start": v(-43, 3) * mm, "end": v(-41, 3) * mm});
            skLineSegment(sketch, "E75.left", {"start": v(-43, 135) * mm, "end": v(-43, 3) * mm});
            skLineSegment(sketch, "E75.right", {"start": v(-41, 135) * mm, "end": v(-41, 3) * mm});
            skLineSegment(sketch, "E76.bottom", {"start": v(-39, 135) * mm, "end": v(-37, 135) * mm});
            skLineSegment(sketch, "E76.top", {"start": v(-39, 3) * mm, "end": v(-37, 3) * mm});
            skLineSegment(sketch, "E76.left", {"start": v(-39, 135) * mm, "end": v(-39, 3) * mm});
            skLineSegment(sketch, "E76.right", {"start": v(-37, 135) * mm, "end": v(-37, 3) * mm});
            skLineSegment(sketch, "E77.bottom", {"start": v(-35, 135) * mm, "end": v(-33, 135) * mm});
            skLineSegment(sketch, "E77.top", {"start": v(-35, 3) * mm, "end": v(-33, 3) * mm});
            skLineSegment(sketch, "E77.left", {"start": v(-35, 135) * mm, "end": v(-35, 3) * mm});
            skLineSegment(sketch, "E77.right", {"start": v(-33, 135) * mm, "end": v(-33, 3) * mm});
            skLineSegment(sketch, "E78.bottom", {"start": v(-31, 135) * mm, "end": v(-29, 135) * mm});
            skLineSegment(sketch, "E78.top", {"start": v(-31, 3) * mm, "end": v(-29, 3) * mm});
            skLineSegment(sketch, "E78.left", {"start": v(-31, 135) * mm, "end": v(-31, 3) * mm});
            skLineSegment(sketch, "E78.right", {"start": v(-29, 135) * mm, "end": v(-29, 3) * mm});
            skLineSegment(sketch, "E79.bottom", {"start": v(-27, 135) * mm, "end": v(-25, 135) * mm});
            skLineSegment(sketch, "E79.top", {"start": v(-27, 3) * mm, "end": v(-25, 3) * mm});
            skLineSegment(sketch, "E79.left", {"start": v(-27, 135) * mm, "end": v(-27, 3) * mm});
            skLineSegment(sketch, "E79.right", {"start": v(-25, 135) * mm, "end": v(-25, 3) * mm});
            skLineSegment(sketch, "E80.bottom", {"start": v(-23, 135) * mm, "end": v(-21, 135) * mm});
            skLineSegment(sketch, "E80.top", {"start": v(-23, 3) * mm, "end": v(-21, 3) * mm});
            skLineSegment(sketch, "E80.left", {"start": v(-23, 135) * mm, "end": v(-23, 3) * mm});
            skLineSegment(sketch, "E80.right", {"start": v(-21, 135) * mm, "end": v(-21, 3) * mm});
            skLineSegment(sketch, "E81.bottom", {"start": v(-19, 135) * mm, "end": v(-17, 135) * mm});
            skLineSegment(sketch, "E81.top", {"start": v(-19, 3) * mm, "end": v(-17, 3) * mm});
            skLineSegment(sketch, "E81.left", {"start": v(-19, 135) * mm, "end": v(-19, 3) * mm});
            skLineSegment(sketch, "E81.right", {"start": v(-17, 135) * mm, "end": v(-17, 3) * mm});
            skLineSegment(sketch, "E82.bottom", {"start": v(-15, 135) * mm, "end": v(-13, 135) * mm});
            skLineSegment(sketch, "E82.top", {"start": v(-15, 3) * mm, "end": v(-13, 3) * mm});
            skLineSegment(sketch, "E82.left", {"start": v(-15, 135) * mm, "end": v(-15, 3) * mm});
            skLineSegment(sketch, "E82.right", {"start": v(-13, 135) * mm, "end": v(-13, 3) * mm});
            skLineSegment(sketch, "E83.bottom", {"start": v(-11, 135) * mm, "end": v(-9, 135) * mm});
            skLineSegment(sketch, "E83.top", {"start": v(-11, 3) * mm, "end": v(-9, 3) * mm});
            skLineSegment(sketch, "E83.left", {"start": v(-11, 135) * mm, "end": v(-11, 3) * mm});
            skLineSegment(sketch, "E83.right", {"start": v(-9, 135) * mm, "end": v(-9, 3) * mm});
            skLineSegment(sketch, "E84.bottom", {"start": v(-7, 135) * mm, "end": v(-5, 135) * mm});
            skLineSegment(sketch, "E84.top", {"start": v(-7, 3) * mm, "end": v(-5, 3) * mm});
            skLineSegment(sketch, "E84.left", {"start": v(-7, 135) * mm, "end": v(-7, 3) * mm});
            skLineSegment(sketch, "E84.right", {"start": v(-5, 135) * mm, "end": v(-5, 3) * mm});
            skLineSegment(sketch, "E85.bottom", {"start": v(1, 135) * mm, "end": v(3, 135) * mm});
            skLineSegment(sketch, "E85.top", {"start": v(1, 3) * mm, "end": v(3, 3) * mm});
            skLineSegment(sketch, "E85.left", {"start": v(1, 135) * mm, "end": v(1, 3) * mm});
            skLineSegment(sketch, "E85.right", {"start": v(3, 135) * mm, "end": v(3, 3) * mm});
            skLineSegment(sketch, "E86.bottom", {"start": v(-3, 135) * mm, "end": v(-1, 135) * mm});
            skLineSegment(sketch, "E86.top", {"start": v(-3, 3) * mm, "end": v(-1, 3) * mm});
            skLineSegment(sketch, "E86.left", {"start": v(-3, 135) * mm, "end": v(-3, 3) * mm});
            skLineSegment(sketch, "E86.right", {"start": v(-1, 135) * mm, "end": v(-1, 3) * mm});
            skLineSegment(sketch, "E87.bottom", {"start": v(5, 135) * mm, "end": v(7, 135) * mm});
            skLineSegment(sketch, "E87.top", {"start": v(5, 3) * mm, "end": v(7, 3) * mm});
            skLineSegment(sketch, "E87.left", {"start": v(5, 135) * mm, "end": v(5, 3) * mm});
            skLineSegment(sketch, "E87.right", {"start": v(7, 135) * mm, "end": v(7, 3) * mm});
            skLineSegment(sketch, "E88.bottom", {"start": v(9, 135) * mm, "end": v(11, 135) * mm});
            skLineSegment(sketch, "E88.top", {"start": v(9, 3) * mm, "end": v(11, 3) * mm});
            skLineSegment(sketch, "E88.left", {"start": v(9, 135) * mm, "end": v(9, 3) * mm});
            skLineSegment(sketch, "E88.right", {"start": v(11, 135) * mm, "end": v(11, 3) * mm});
            skLineSegment(sketch, "E89.bottom", {"start": v(13, 135) * mm, "end": v(15, 135) * mm});
            skLineSegment(sketch, "E89.top", {"start": v(13, 3) * mm, "end": v(15, 3) * mm});
            skLineSegment(sketch, "E89.left", {"start": v(13, 135) * mm, "end": v(13, 3) * mm});
            skLineSegment(sketch, "E89.right", {"start": v(15, 135) * mm, "end": v(15, 3) * mm});
            skLineSegment(sketch, "E90.bottom", {"start": v(17, 135) * mm, "end": v(19, 135) * mm});
            skLineSegment(sketch, "E90.top", {"start": v(17, 3) * mm, "end": v(19, 3) * mm});
            skLineSegment(sketch, "E90.left", {"start": v(17, 135) * mm, "end": v(17, 3) * mm});
            skLineSegment(sketch, "E90.right", {"start": v(19, 135) * mm, "end": v(19, 3) * mm});
            skLineSegment(sketch, "E91.bottom", {"start": v(21, 135) * mm, "end": v(23, 135) * mm});
            skLineSegment(sketch, "E91.top", {"start": v(21, 3) * mm, "end": v(23, 3) * mm});
            skLineSegment(sketch, "E91.left", {"start": v(21, 135) * mm, "end": v(21, 3) * mm});
            skLineSegment(sketch, "E91.right", {"start": v(23, 135) * mm, "end": v(23, 3) * mm});
            skLineSegment(sketch, "E92.bottom", {"start": v(25, 135) * mm, "end": v(27, 135) * mm});
            skLineSegment(sketch, "E92.top", {"start": v(25, 3) * mm, "end": v(27, 3) * mm});
            skLineSegment(sketch, "E92.left", {"start": v(25, 135) * mm, "end": v(25, 3) * mm});
            skLineSegment(sketch, "E92.right", {"start": v(27, 135) * mm, "end": v(27, 3) * mm});
            skLineSegment(sketch, "E93.bottom", {"start": v(29, 135) * mm, "end": v(31, 135) * mm});
            skLineSegment(sketch, "E93.top", {"start": v(29, 3) * mm, "end": v(31, 3) * mm});
            skLineSegment(sketch, "E93.left", {"start": v(29, 135) * mm, "end": v(29, 3) * mm});
            skLineSegment(sketch, "E93.right", {"start": v(31, 135) * mm, "end": v(31, 3) * mm});
            skLineSegment(sketch, "E94.bottom", {"start": v(33, 135) * mm, "end": v(35, 135) * mm});
            skLineSegment(sketch, "E94.top", {"start": v(33, 3) * mm, "end": v(35, 3) * mm});
            skLineSegment(sketch, "E94.left", {"start": v(33, 135) * mm, "end": v(33, 3) * mm});
            skLineSegment(sketch, "E94.right", {"start": v(35, 135) * mm, "end": v(35, 3) * mm});
            skLineSegment(sketch, "E95.bottom", {"start": v(37, 135) * mm, "end": v(39, 135) * mm});
            skLineSegment(sketch, "E95.top", {"start": v(37, 3) * mm, "end": v(39, 3) * mm});
            skLineSegment(sketch, "E95.left", {"start": v(37, 135) * mm, "end": v(37, 3) * mm});
            skLineSegment(sketch, "E95.right", {"start": v(39, 135) * mm, "end": v(39, 3) * mm});
            skLineSegment(sketch, "E96.bottom", {"start": v(41, 135) * mm, "end": v(43, 135) * mm});
            skLineSegment(sketch, "E96.top", {"start": v(41, 3) * mm, "end": v(43, 3) * mm});
            skLineSegment(sketch, "E96.left", {"start": v(41, 135) * mm, "end": v(41, 3) * mm});
            skLineSegment(sketch, "E96.right", {"start": v(43, 135) * mm, "end": v(43, 3) * mm});
            skLineSegment(sketch, "E97.bottom", {"start": v(45, 135) * mm, "end": v(47, 135) * mm});
            skLineSegment(sketch, "E97.top", {"start": v(45, 3) * mm, "end": v(47, 3) * mm});
            skLineSegment(sketch, "E97.left", {"start": v(45, 135) * mm, "end": v(45, 3) * mm});
            skLineSegment(sketch, "E97.right", {"start": v(47, 135) * mm, "end": v(47, 3) * mm});
            skLineSegment(sketch, "E98.bottom", {"start": v(49, 135) * mm, "end": v(51, 135) * mm});
            skLineSegment(sketch, "E98.top", {"start": v(49, 3) * mm, "end": v(51, 3) * mm});
            skLineSegment(sketch, "E98.left", {"start": v(49, 135) * mm, "end": v(49, 3) * mm});
            skLineSegment(sketch, "E98.right", {"start": v(51, 135) * mm, "end": v(51, 3) * mm});
            skLineSegment(sketch, "E99.bottom", {"start": v(53, 135) * mm, "end": v(55, 135) * mm});
            skLineSegment(sketch, "E99.top", {"start": v(53, 3) * mm, "end": v(55, 3) * mm});
            skLineSegment(sketch, "E99.left", {"start": v(53, 135) * mm, "end": v(53, 3) * mm});
            skLineSegment(sketch, "E99.right", {"start": v(55, 135) * mm, "end": v(55, 3) * mm});
            skLineSegment(sketch, "E100.bottom", {"start": v(57, 135) * mm, "end": v(59, 135) * mm});
            skLineSegment(sketch, "E100.top", {"start": v(57, 3) * mm, "end": v(59, 3) * mm});
            skLineSegment(sketch, "E100.left", {"start": v(57, 135) * mm, "end": v(57, 3) * mm});
            skLineSegment(sketch, "E100.right", {"start": v(59, 135) * mm, "end": v(59, 3) * mm});
            skLineSegment(sketch, "E101.bottom", {"start": v(61, 135) * mm, "end": v(63, 135) * mm});
            skLineSegment(sketch, "E101.top", {"start": v(61, 3) * mm, "end": v(63, 3) * mm});
            skLineSegment(sketch, "E101.left", {"start": v(61, 135) * mm, "end": v(61, 3) * mm});
            skLineSegment(sketch, "E101.right", {"start": v(63, 135) * mm, "end": v(63, 3) * mm});
            skSolve(sketch);
        }
        {
            var Q0;
            Q0 = qSketchRegion(id + "F11", true);
            extrude(context, id + "F12", {"entities" : qUnion([Q0]), "operationType" : NewBodyOperationType.REMOVE, "oppositeDirection" : true, "depth" : 3 * mm, "offsetDistance" : 25 * mm});
        }
        {
            var Q0;
            Q0=makeQuery(id+"F5.boolean.opBoolean","MERGE",FACE,{"derivedFrom":[makeQuery(id+"F1.opExtrude","SWEPT_FACE",FACE,{"disambiguationData":[OSD([sQuery(id+"F0.wireOp",EDGE,"E0.left")])]}),makeQuery(id+"F5.opExtrude","SWEPT_FACE",FACE,{"disambiguationData":[OSD([sQuery(id+"F4.wireOp",EDGE,"E3.left")])]})]});
            var sketch = newSketch(context, id + "F13", { "sketchPlane" : qUnion([Q0])});
            skLineSegment(sketch, "E102.bottom", {"start": v(-63, 135) * mm, "end": v(-61, 135) * mm});
            skLineSegment(sketch, "E102.top", {"start": v(-63, 3) * mm, "end": v(-61, 3) * mm});
            skLineSegment(sketch, "E102.left", {"start": v(-63, 135) * mm, "end": v(-63, 3) * mm});
            skLineSegment(sketch, "E102.right", {"start": v(-61, 135) * mm, "end": v(-61, 3) * mm});
            skLineSegment(sketch, "E103.bottom", {"start": v(-59, 135) * mm, "end": v(-57, 135) * mm});
            skLineSegment(sketch, "E103.top", {"start": v(-59, 3) * mm, "end": v(-57, 3) * mm});
            skLineSegment(sketch, "E103.left", {"start": v(-59, 135) * mm, "end": v(-59, 3) * mm});
            skLineSegment(sketch, "E103.right", {"start": v(-57, 135) * mm, "end": v(-57, 3) * mm});
            skLineSegment(sketch, "E104.bottom", {"start": v(-55, 135) * mm, "end": v(-53, 135) * mm});
            skLineSegment(sketch, "E104.top", {"start": v(-55, 3) * mm, "end": v(-53, 3) * mm});
            skLineSegment(sketch, "E104.left", {"start": v(-55, 135) * mm, "end": v(-55, 3) * mm});
            skLineSegment(sketch, "E104.right", {"start": v(-53, 135) * mm, "end": v(-53, 3) * mm});
            skLineSegment(sketch, "E105.bottom", {"start": v(-51, 135) * mm, "end": v(-49, 135) * mm});
            skLineSegment(sketch, "E105.top", {"start": v(-51, 3) * mm, "end": v(-49, 3) * mm});
            skLineSegment(sketch, "E105.left", {"start": v(-51, 135) * mm, "end": v(-51, 3) * mm});
            skLineSegment(sketch, "E105.right", {"start": v(-49, 135) * mm, "end": v(-49, 3) * mm});
            skLineSegment(sketch, "E106.bottom", {"start": v(-47, 135) * mm, "end": v(-45, 135) * mm});
            skLineSegment(sketch, "E106.top", {"start": v(-47, 3) * mm, "end": v(-45, 3) * mm});
            skLineSegment(sketch, "E106.left", {"start": v(-47, 135) * mm, "end": v(-47, 3) * mm});
            skLineSegment(sketch, "E106.right", {"start": v(-45, 135) * mm, "end": v(-45, 3) * mm});
            skLineSegment(sketch, "E107.bottom", {"start": v(-43, 135) * mm, "end": v(-41, 135) * mm});
            skLineSegment(sketch, "E107.top", {"start": v(-43, 3) * mm, "end": v(-41, 3) * mm});
            skLineSegment(sketch, "E107.left", {"start": v(-43, 135) * mm, "end": v(-43, 3) * mm});
            skLineSegment(sketch, "E107.right", {"start": v(-41, 135) * mm, "end": v(-41, 3) * mm});
            skLineSegment(sketch, "E108.bottom", {"start": v(-39, 135) * mm, "end": v(-37, 135) * mm});
            skLineSegment(sketch, "E108.top", {"start": v(-39, 3) * mm, "end": v(-37, 3) * mm});
            skLineSegment(sketch, "E108.left", {"start": v(-39, 135) * mm, "end": v(-39, 3) * mm});
            skLineSegment(sketch, "E108.right", {"start": v(-37, 135) * mm, "end": v(-37, 3) * mm});
            skLineSegment(sketch, "E109.bottom", {"start": v(-35, 135) * mm, "end": v(-33, 135) * mm});
            skLineSegment(sketch, "E109.top", {"start": v(-35, 3) * mm, "end": v(-33, 3) * mm});
            skLineSegment(sketch, "E109.left", {"start": v(-35, 135) * mm, "end": v(-35, 3) * mm});
            skLineSegment(sketch, "E109.right", {"start": v(-33, 135) * mm, "end": v(-33, 3) * mm});
            skLineSegment(sketch, "E110.bottom", {"start": v(-31, 135) * mm, "end": v(-29, 135) * mm});
            skLineSegment(sketch, "E110.top", {"start": v(-31, 3) * mm, "end": v(-29, 3) * mm});
            skLineSegment(sketch, "E110.left", {"start": v(-31, 135) * mm, "end": v(-31, 3) * mm});
            skLineSegment(sketch, "E110.right", {"start": v(-29, 135) * mm, "end": v(-29, 3) * mm});
            skLineSegment(sketch, "E111.bottom", {"start": v(-27, 135) * mm, "end": v(-25, 135) * mm});
            skLineSegment(sketch, "E111.top", {"start": v(-27, 3) * mm, "end": v(-25, 3) * mm});
            skLineSegment(sketch, "E111.left", {"start": v(-27, 135) * mm, "end": v(-27, 3) * mm});
            skLineSegment(sketch, "E111.right", {"start": v(-25, 135) * mm, "end": v(-25, 3) * mm});
            skLineSegment(sketch, "E112.bottom", {"start": v(-23, 135) * mm, "end": v(-21, 135) * mm});
            skLineSegment(sketch, "E112.top", {"start": v(-23, 3) * mm, "end": v(-21, 3) * mm});
            skLineSegment(sketch, "E112.left", {"start": v(-23, 135) * mm, "end": v(-23, 3) * mm});
            skLineSegment(sketch, "E112.right", {"start": v(-21, 135) * mm, "end": v(-21, 3) * mm});
            skLineSegment(sketch, "E113.bottom", {"start": v(-19, 135) * mm, "end": v(-17, 135) * mm});
            skLineSegment(sketch, "E113.top", {"start": v(-19, 3) * mm, "end": v(-17, 3) * mm});
            skLineSegment(sketch, "E113.left", {"start": v(-19, 135) * mm, "end": v(-19, 3) * mm});
            skLineSegment(sketch, "E113.right", {"start": v(-17, 135) * mm, "end": v(-17, 3) * mm});
            skLineSegment(sketch, "E114.bottom", {"start": v(-15, 135) * mm, "end": v(-13, 135) * mm});
            skLineSegment(sketch, "E114.top", {"start": v(-15, 3) * mm, "end": v(-13, 3) * mm});
            skLineSegment(sketch, "E114.left", {"start": v(-15, 135) * mm, "end": v(-15, 3) * mm});
            skLineSegment(sketch, "E114.right", {"start": v(-13, 135) * mm, "end": v(-13, 3) * mm});
            skLineSegment(sketch, "E115.bottom", {"start": v(-11, 135) * mm, "end": v(-9, 135) * mm});
            skLineSegment(sketch, "E115.top", {"start": v(-11, 3) * mm, "end": v(-9, 3) * mm});
            skLineSegment(sketch, "E115.left", {"start": v(-11, 135) * mm, "end": v(-11, 3) * mm});
            skLineSegment(sketch, "E115.right", {"start": v(-9, 135) * mm, "end": v(-9, 3) * mm});
            skLineSegment(sketch, "E116.bottom", {"start": v(-7, 135) * mm, "end": v(-5, 135) * mm});
            skLineSegment(sketch, "E116.top", {"start": v(-7, 3) * mm, "end": v(-5, 3) * mm});
            skLineSegment(sketch, "E116.left", {"start": v(-7, 135) * mm, "end": v(-7, 3) * mm});
            skLineSegment(sketch, "E116.right", {"start": v(-5, 135) * mm, "end": v(-5, 3) * mm});
            skLineSegment(sketch, "E117.bottom", {"start": v(-3, 135) * mm, "end": v(-1, 135) * mm});
            skLineSegment(sketch, "E117.top", {"start": v(-3, 3) * mm, "end": v(-1, 3) * mm});
            skLineSegment(sketch, "E117.left", {"start": v(-3, 135) * mm, "end": v(-3, 3) * mm});
            skLineSegment(sketch, "E117.right", {"start": v(-1, 135) * mm, "end": v(-1, 3) * mm});
            skLineSegment(sketch, "E118.bottom", {"start": v(1, 135) * mm, "end": v(3, 135) * mm});
            skLineSegment(sketch, "E118.top", {"start": v(1, 3) * mm, "end": v(3, 3) * mm});
            skLineSegment(sketch, "E118.left", {"start": v(1, 135) * mm, "end": v(1, 3) * mm});
            skLineSegment(sketch, "E118.right", {"start": v(3, 135) * mm, "end": v(3, 3) * mm});
            skLineSegment(sketch, "E119.bottom", {"start": v(5, 135) * mm, "end": v(7, 135) * mm});
            skLineSegment(sketch, "E119.top", {"start": v(5, 3) * mm, "end": v(7, 3) * mm});
            skLineSegment(sketch, "E119.left", {"start": v(5, 135) * mm, "end": v(5, 3) * mm});
            skLineSegment(sketch, "E119.right", {"start": v(7, 135) * mm, "end": v(7, 3) * mm});
            skLineSegment(sketch, "E120.bottom", {"start": v(9, 135) * mm, "end": v(11, 135) * mm});
            skLineSegment(sketch, "E120.top", {"start": v(9, 3) * mm, "end": v(11, 3) * mm});
            skLineSegment(sketch, "E120.left", {"start": v(9, 135) * mm, "end": v(9, 3) * mm});
            skLineSegment(sketch, "E120.right", {"start": v(11, 135) * mm, "end": v(11, 3) * mm});
            skLineSegment(sketch, "E121.bottom", {"start": v(13, 135) * mm, "end": v(15, 135) * mm});
            skLineSegment(sketch, "E121.top", {"start": v(13, 3) * mm, "end": v(15, 3) * mm});
            skLineSegment(sketch, "E121.left", {"start": v(13, 135) * mm, "end": v(13, 3) * mm});
            skLineSegment(sketch, "E121.right", {"start": v(15, 135) * mm, "end": v(15, 3) * mm});
            skLineSegment(sketch, "E122.bottom", {"start": v(17, 135) * mm, "end": v(19, 135) * mm});
            skLineSegment(sketch, "E122.top", {"start": v(17, 3) * mm, "end": v(19, 3) * mm});
            skLineSegment(sketch, "E122.left", {"start": v(17, 135) * mm, "end": v(17, 3) * mm});
            skLineSegment(sketch, "E122.right", {"start": v(19, 135) * mm, "end": v(19, 3) * mm});
            skLineSegment(sketch, "E123.bottom", {"start": v(21, 135) * mm, "end": v(23, 135) * mm});
            skLineSegment(sketch, "E123.top", {"start": v(21, 3) * mm, "end": v(23, 3) * mm});
            skLineSegment(sketch, "E123.left", {"start": v(21, 135) * mm, "end": v(21, 3) * mm});
            skLineSegment(sketch, "E123.right", {"start": v(23, 135) * mm, "end": v(23, 3) * mm});
            skLineSegment(sketch, "E124.bottom", {"start": v(25, 135) * mm, "end": v(27, 135) * mm});
            skLineSegment(sketch, "E124.top", {"start": v(25, 3) * mm, "end": v(27, 3) * mm});
            skLineSegment(sketch, "E124.left", {"start": v(25, 135) * mm, "end": v(25, 3) * mm});
            skLineSegment(sketch, "E124.right", {"start": v(27, 135) * mm, "end": v(27, 3) * mm});
            skLineSegment(sketch, "E125.bottom", {"start": v(29, 135) * mm, "end": v(31, 135) * mm});
            skLineSegment(sketch, "E125.top", {"start": v(29, 3) * mm, "end": v(31, 3) * mm});
            skLineSegment(sketch, "E125.left", {"start": v(29, 135) * mm, "end": v(29, 3) * mm});
            skLineSegment(sketch, "E125.right", {"start": v(31, 135) * mm, "end": v(31, 3) * mm});
            skLineSegment(sketch, "E126.bottom", {"start": v(33, 135) * mm, "end": v(35, 135) * mm});
            skLineSegment(sketch, "E126.top", {"start": v(33, 3) * mm, "end": v(35, 3) * mm});
            skLineSegment(sketch, "E126.left", {"start": v(33, 135) * mm, "end": v(33, 3) * mm});
            skLineSegment(sketch, "E126.right", {"start": v(35, 135) * mm, "end": v(35, 3) * mm});
            skLineSegment(sketch, "E127.bottom", {"start": v(37, 135) * mm, "end": v(39, 135) * mm});
            skLineSegment(sketch, "E127.top", {"start": v(37, 3) * mm, "end": v(39, 3) * mm});
            skLineSegment(sketch, "E127.left", {"start": v(37, 135) * mm, "end": v(37, 3) * mm});
            skLineSegment(sketch, "E127.right", {"start": v(39, 135) * mm, "end": v(39, 3) * mm});
            skLineSegment(sketch, "E128.bottom", {"start": v(41, 135) * mm, "end": v(43, 135) * mm});
            skLineSegment(sketch, "E128.top", {"start": v(41, 3) * mm, "end": v(43, 3) * mm});
            skLineSegment(sketch, "E128.left", {"start": v(41, 135) * mm, "end": v(41, 3) * mm});
            skLineSegment(sketch, "E128.right", {"start": v(43, 135) * mm, "end": v(43, 3) * mm});
            skLineSegment(sketch, "E129.bottom", {"start": v(45, 135) * mm, "end": v(47, 135) * mm});
            skLineSegment(sketch, "E129.top", {"start": v(45, 3) * mm, "end": v(47, 3) * mm});
            skLineSegment(sketch, "E129.left", {"start": v(45, 135) * mm, "end": v(45, 3) * mm});
            skLineSegment(sketch, "E129.right", {"start": v(47, 135) * mm, "end": v(47, 3) * mm});
            skLineSegment(sketch, "E130.bottom", {"start": v(49, 135) * mm, "end": v(51, 135) * mm});
            skLineSegment(sketch, "E130.top", {"start": v(49, 3) * mm, "end": v(51, 3) * mm});
            skLineSegment(sketch, "E130.left", {"start": v(49, 135) * mm, "end": v(49, 3) * mm});
            skLineSegment(sketch, "E130.right", {"start": v(51, 135) * mm, "end": v(51, 3) * mm});
            skLineSegment(sketch, "E131.bottom", {"start": v(53, 135) * mm, "end": v(55, 135) * mm});
            skLineSegment(sketch, "E131.top", {"start": v(53, 3) * mm, "end": v(55, 3) * mm});
            skLineSegment(sketch, "E131.left", {"start": v(53, 135) * mm, "end": v(53, 3) * mm});
            skLineSegment(sketch, "E131.right", {"start": v(55, 135) * mm, "end": v(55, 3) * mm});
            skLineSegment(sketch, "E132.bottom", {"start": v(57, 135) * mm, "end": v(59, 135) * mm});
            skLineSegment(sketch, "E132.top", {"start": v(57, 3) * mm, "end": v(59, 3) * mm});
            skLineSegment(sketch, "E132.left", {"start": v(57, 135) * mm, "end": v(57, 3) * mm});
            skLineSegment(sketch, "E132.right", {"start": v(59, 135) * mm, "end": v(59, 3) * mm});
            skLineSegment(sketch, "E133.bottom", {"start": v(61, 135) * mm, "end": v(63, 135) * mm});
            skLineSegment(sketch, "E133.top", {"start": v(61, 3) * mm, "end": v(63, 3) * mm});
            skLineSegment(sketch, "E133.left", {"start": v(61, 135) * mm, "end": v(61, 3) * mm});
            skLineSegment(sketch, "E133.right", {"start": v(63, 135) * mm, "end": v(63, 3) * mm});
            skSolve(sketch);
        }
        {
            var Q0;
            Q0 = qSketchRegion(id + "F13", true);
            extrude(context, id + "F14", {"entities" : qUnion([Q0]), "operationType" : NewBodyOperationType.REMOVE, "oppositeDirection" : true, "depth" : 3 * mm, "offsetDistance" : 25 * mm});
        }
        {
            var Q0;
            {var subQ0=sQuery(id+"F0.wireOp",EDGE,"E0.left");var subQ1=sQuery(id+"F0.wireOp",EDGE,"E0.top");var subQ2=sQuery(id+"F0.wireOp",EDGE,"E0.right");var subQ3=sQuery(id+"F0.wireOp",EDGE,"E0.bottom");Q0=makeQuery(id+"F14.boolean.opBoolean","MERGE",FACE,{"derivedFrom":[makeQuery(id+"F12.boolean.opBoolean","MERGE",FACE,{"derivedFrom":[makeQuery(id+"F10.boolean.opBoolean","MERGE",FACE,{"derivedFrom":[makeQuery(id+"F8.boolean.opBoolean","MERGE",FACE,{"derivedFrom":[makeQuery(id+"F3.boolean.opBoolean","SPLIT",FACE,{"disambiguationData":[TD([makeQuery(id+"F1.opExtrude","SWEPT_FACE",FACE,{"disambiguationData":[OSD([subQ3])]})])],"derivedFrom":makeQuery(id+"F1.opExtrude","CAP_FACE",FACE,{"disambiguationData":[OSD([subQ3,subQ1,subQ0,subQ2])],"isStart":false})}),makeQuery(id+"F8.opExtrude","SWEPT_FACE",FACE,{"disambiguationData":[OSD([sQuery(id+"F7.wireOp",EDGE,"E5.top")])]}),makeQuery(id+"F8.opExtrude","SWEPT_FACE",FACE,{"disambiguationData":[OSD([sQuery(id+"F7.wireOp",EDGE,"E6.top")])]}),makeQuery(id+"F8.opExtrude","SWEPT_FACE",FACE,{"disambiguationData":[OSD([sQuery(id+"F7.wireOp",EDGE,"E7.top")])]}),makeQuery(id+"F8.opExtrude","SWEPT_FACE",FACE,{"disambiguationData":[OSD([sQuery(id+"F7.wireOp",EDGE,"E8.top")])]}),makeQuery(id+"F8.opExtrude","SWEPT_FACE",FACE,{"disambiguationData":[OSD([sQuery(id+"F7.wireOp",EDGE,"E9.top")])]}),makeQuery(id+"F8.opExtrude","SWEPT_FACE",FACE,{"disambiguationData":[OSD([sQuery(id+"F7.wireOp",EDGE,"E10.top")])]}),makeQuery(id+"F8.opExtrude","SWEPT_FACE",FACE,{"disambiguationData":[OSD([sQuery(id+"F7.wireOp",EDGE,"E11.top")])]}),makeQuery(id+"F8.opExtrude","SWEPT_FACE",FACE,{"disambiguationData":[OSD([sQuery(id+"F7.wireOp",EDGE,"E12.top")])]}),makeQuery(id+"F8.opExtrude","SWEPT_FACE",FACE,{"disambiguationData":[OSD([sQuery(id+"F7.wireOp",EDGE,"E13.top")])]}),makeQuery(id+"F8.opExtrude","SWEPT_FACE",FACE,{"disambiguationData":[OSD([sQuery(id+"F7.wireOp",EDGE,"E14.top")])]}),makeQuery(id+"F8.opExtrude","SWEPT_FACE",FACE,{"disambiguationData":[OSD([sQuery(id+"F7.wireOp",EDGE,"E15.top")])]}),makeQuery(id+"F8.opExtrude","SWEPT_FACE",FACE,{"disambiguationData":[OSD([sQuery(id+"F7.wireOp",EDGE,"E16.bottom")])]}),makeQuery(id+"F8.opExtrude","SWEPT_FACE",FACE,{"disambiguationData":[OSD([sQuery(id+"F7.wireOp",EDGE,"E17.top")])]}),makeQuery(id+"F8.opExtrude","SWEPT_FACE",FACE,{"disambiguationData":[OSD([sQuery(id+"F7.wireOp",EDGE,"E18.bottom")])]}),makeQuery(id+"F8.opExtrude","SWEPT_FACE",FACE,{"disambiguationData":[OSD([sQuery(id+"F7.wireOp",EDGE,"E19.top")])]}),makeQuery(id+"F8.opExtrude","SWEPT_FACE",FACE,{"disambiguationData":[OSD([sQuery(id+"F7.wireOp",EDGE,"E20.bottom")])]}),makeQuery(id+"F8.opExtrude","SWEPT_FACE",FACE,{"disambiguationData":[OSD([sQuery(id+"F7.wireOp",EDGE,"E21.top")])]}),makeQuery(id+"F8.opExtrude","SWEPT_FACE",FACE,{"disambiguationData":[OSD([sQuery(id+"F7.wireOp",EDGE,"E22.bottom")])]}),makeQuery(id+"F8.opExtrude","SWEPT_FACE",FACE,{"disambiguationData":[OSD([sQuery(id+"F7.wireOp",EDGE,"E23.top")])]}),makeQuery(id+"F8.opExtrude","SWEPT_FACE",FACE,{"disambiguationData":[OSD([sQuery(id+"F7.wireOp",EDGE,"E24.bottom")])]}),makeQuery(id+"F8.opExtrude","SWEPT_FACE",FACE,{"disambiguationData":[OSD([sQuery(id+"F7.wireOp",EDGE,"E25.top")])]}),makeQuery(id+"F8.opExtrude","SWEPT_FACE",FACE,{"disambiguationData":[OSD([sQuery(id+"F7.wireOp",EDGE,"E26.top")])]}),makeQuery(id+"F8.opExtrude","SWEPT_FACE",FACE,{"disambiguationData":[OSD([sQuery(id+"F7.wireOp",EDGE,"E27.bottom")])]}),makeQuery(id+"F8.opExtrude","SWEPT_FACE",FACE,{"disambiguationData":[OSD([sQuery(id+"F7.wireOp",EDGE,"E28.top")])]}),makeQuery(id+"F8.opExtrude","SWEPT_FACE",FACE,{"disambiguationData":[OSD([sQuery(id+"F7.wireOp",EDGE,"E29.bottom")])]}),makeQuery(id+"F8.opExtrude","SWEPT_FACE",FACE,{"disambiguationData":[OSD([sQuery(id+"F7.wireOp",EDGE,"E30.top")])]}),makeQuery(id+"F8.opExtrude","SWEPT_FACE",FACE,{"disambiguationData":[OSD([sQuery(id+"F7.wireOp",EDGE,"E31.bottom")])]}),makeQuery(id+"F8.opExtrude","SWEPT_FACE",FACE,{"disambiguationData":[OSD([sQuery(id+"F7.wireOp",EDGE,"E32.top")])]}),makeQuery(id+"F8.opExtrude","SWEPT_FACE",FACE,{"disambiguationData":[OSD([sQuery(id+"F7.wireOp",EDGE,"E33.bottom")])]}),makeQuery(id+"F8.opExtrude","SWEPT_FACE",FACE,{"disambiguationData":[OSD([sQuery(id+"F7.wireOp",EDGE,"E34.top")])]}),makeQuery(id+"F8.opExtrude","SWEPT_FACE",FACE,{"disambiguationData":[OSD([sQuery(id+"F7.wireOp",EDGE,"E35.top")])]}),makeQuery(id+"F8.opExtrude","SWEPT_FACE",FACE,{"disambiguationData":[OSD([sQuery(id+"F7.wireOp",EDGE,"E36.top")])]})]}),makeQuery(id+"F10.opExtrude","SWEPT_FACE",FACE,{"disambiguationData":[OSD([sQuery(id+"F9.wireOp",EDGE,"E37.top")])]}),makeQuery(id+"F10.opExtrude","SWEPT_FACE",FACE,{"disambiguationData":[OSD([sQuery(id+"F9.wireOp",EDGE,"E38.top")])]}),makeQuery(id+"F10.opExtrude","SWEPT_FACE",FACE,{"disambiguationData":[OSD([sQuery(id+"F9.wireOp",EDGE,"E39.top")])]}),makeQuery(id+"F10.opExtrude","SWEPT_FACE",FACE,{"disambiguationData":[OSD([sQuery(id+"F9.wireOp",EDGE,"E40.top")])]}),makeQuery(id+"F10.opExtrude","SWEPT_FACE",FACE,{"disambiguationData":[OSD([sQuery(id+"F9.wireOp",EDGE,"E41.top")])]}),makeQuery(id+"F10.opExtrude","SWEPT_FACE",FACE,{"disambiguationData":[OSD([sQuery(id+"F9.wireOp",EDGE,"E42.top")])]}),makeQuery(id+"F10.opExtrude","SWEPT_FACE",FACE,{"disambiguationData":[OSD([sQuery(id+"F9.wireOp",EDGE,"E43.top")])]}),makeQuery(id+"F10.opExtrude","SWEPT_FACE",FACE,{"disambiguationData":[OSD([sQuery(id+"F9.wireOp",EDGE,"E44.top")])]}),makeQuery(id+"F10.opExtrude","SWEPT_FACE",FACE,{"disambiguationData":[OSD([sQuery(id+"F9.wireOp",EDGE,"E45.top")])]}),makeQuery(id+"F10.opExtrude","SWEPT_FACE",FACE,{"disambiguationData":[OSD([sQuery(id+"F9.wireOp",EDGE,"E46.top")])]}),makeQuery(id+"F10.opExtrude","SWEPT_FACE",FACE,{"disambiguationData":[OSD([sQuery(id+"F9.wireOp",EDGE,"E47.top")])]}),makeQuery(id+"F10.opExtrude","SWEPT_FACE",FACE,{"disambiguationData":[OSD([sQuery(id+"F9.wireOp",EDGE,"E48.top")])]}),makeQuery(id+"F10.opExtrude","SWEPT_FACE",FACE,{"disambiguationData":[OSD([sQuery(id+"F9.wireOp",EDGE,"E50.top")])]}),makeQuery(id+"F10.opExtrude","SWEPT_FACE",FACE,{"disambiguationData":[OSD([sQuery(id+"F9.wireOp",EDGE,"E51.top")])]}),makeQuery(id+"F10.opExtrude","SWEPT_FACE",FACE,{"disambiguationData":[OSD([sQuery(id+"F9.wireOp",EDGE,"E52.top")])]}),makeQuery(id+"F10.opExtrude","SWEPT_FACE",FACE,{"disambiguationData":[OSD([sQuery(id+"F9.wireOp",EDGE,"E53.top")])]}),makeQuery(id+"F10.opExtrude","SWEPT_FACE",FACE,{"disambiguationData":[OSD([sQuery(id+"F9.wireOp",EDGE,"E54.top")])]}),makeQuery(id+"F10.opExtrude","SWEPT_FACE",FACE,{"disambiguationData":[OSD([sQuery(id+"F9.wireOp",EDGE,"E55.top")])]}),makeQuery(id+"F10.opExtrude","SWEPT_FACE",FACE,{"disambiguationData":[OSD([sQuery(id+"F9.wireOp",EDGE,"E56.top")])]}),makeQuery(id+"F10.opExtrude","SWEPT_FACE",FACE,{"disambiguationData":[OSD([sQuery(id+"F9.wireOp",EDGE,"E57.top")])]}),makeQuery(id+"F10.opExtrude","SWEPT_FACE",FACE,{"disambiguationData":[OSD([sQuery(id+"F9.wireOp",EDGE,"E58.top")])]}),makeQuery(id+"F10.opExtrude","SWEPT_FACE",FACE,{"disambiguationData":[OSD([sQuery(id+"F9.wireOp",EDGE,"E59.top")])]}),makeQuery(id+"F10.opExtrude","SWEPT_FACE",FACE,{"disambiguationData":[OSD([sQuery(id+"F9.wireOp",EDGE,"E60.top")])]}),makeQuery(id+"F10.opExtrude","SWEPT_FACE",FACE,{"disambiguationData":[OSD([sQuery(id+"F9.wireOp",EDGE,"E61.top")])]}),makeQuery(id+"F10.opExtrude","SWEPT_FACE",FACE,{"disambiguationData":[OSD([sQuery(id+"F9.wireOp",EDGE,"E62.top")])]}),makeQuery(id+"F10.opExtrude","SWEPT_FACE",FACE,{"disambiguationData":[OSD([sQuery(id+"F9.wireOp",EDGE,"E63.top")])]}),makeQuery(id+"F10.opExtrude","SWEPT_FACE",FACE,{"disambiguationData":[OSD([sQuery(id+"F9.wireOp",EDGE,"E64.top")])]}),makeQuery(id+"F10.opExtrude","SWEPT_FACE",FACE,{"disambiguationData":[OSD([sQuery(id+"F9.wireOp",EDGE,"E65.top")])]}),makeQuery(id+"F10.opExtrude","SWEPT_FACE",FACE,{"disambiguationData":[OSD([sQuery(id+"F9.wireOp",EDGE,"E66.top")])]}),makeQuery(id+"F10.opExtrude","SWEPT_FACE",FACE,{"disambiguationData":[OSD([sQuery(id+"F9.wireOp",EDGE,"E67.top")])]}),makeQuery(id+"F10.opExtrude","SWEPT_FACE",FACE,{"disambiguationData":[OSD([sQuery(id+"F9.wireOp",EDGE,"E68.top")])]}),makeQuery(id+"F10.opExtrude","SWEPT_FACE",FACE,{"disambiguationData":[OSD([sQuery(id+"F9.wireOp",EDGE,"E69.top")])]})]}),makeQuery(id+"F12.opExtrude","SWEPT_FACE",FACE,{"disambiguationData":[OSD([sQuery(id+"F11.wireOp",EDGE,"E70.top")])]}),makeQuery(id+"F12.opExtrude","SWEPT_FACE",FACE,{"disambiguationData":[OSD([sQuery(id+"F11.wireOp",EDGE,"E71.top")])]}),makeQuery(id+"F12.opExtrude","SWEPT_FACE",FACE,{"disambiguationData":[OSD([sQuery(id+"F11.wireOp",EDGE,"E72.top")])]}),makeQuery(id+"F12.opExtrude","SWEPT_FACE",FACE,{"disambiguationData":[OSD([sQuery(id+"F11.wireOp",EDGE,"E73.top")])]}),makeQuery(id+"F12.opExtrude","SWEPT_FACE",FACE,{"disambiguationData":[OSD([sQuery(id+"F11.wireOp",EDGE,"E74.top")])]}),makeQuery(id+"F12.opExtrude","SWEPT_FACE",FACE,{"disambiguationData":[OSD([sQuery(id+"F11.wireOp",EDGE,"E75.top")])]}),makeQuery(id+"F12.opExtrude","SWEPT_FACE",FACE,{"disambiguationData":[OSD([sQuery(id+"F11.wireOp",EDGE,"E76.top")])]}),makeQuery(id+"F12.opExtrude","SWEPT_FACE",FACE,{"disambiguationData":[OSD([sQuery(id+"F11.wireOp",EDGE,"E77.top")])]}),makeQuery(id+"F12.opExtrude","SWEPT_FACE",FACE,{"disambiguationData":[OSD([sQuery(id+"F11.wireOp",EDGE,"E78.top")])]}),makeQuery(id+"F12.opExtrude","SWEPT_FACE",FACE,{"disambiguationData":[OSD([sQuery(id+"F11.wireOp",EDGE,"E79.top")])]}),makeQuery(id+"F12.opExtrude","SWEPT_FACE",FACE,{"disambiguationData":[OSD([sQuery(id+"F11.wireOp",EDGE,"E80.top")])]}),makeQuery(id+"F12.opExtrude","SWEPT_FACE",FACE,{"disambiguationData":[OSD([sQuery(id+"F11.wireOp",EDGE,"E81.top")])]}),makeQuery(id+"F12.opExtrude","SWEPT_FACE",FACE,{"disambiguationData":[OSD([sQuery(id+"F11.wireOp",EDGE,"E82.top")])]}),makeQuery(id+"F12.opExtrude","SWEPT_FACE",FACE,{"disambiguationData":[OSD([sQuery(id+"F11.wireOp",EDGE,"E83.top")])]}),makeQuery(id+"F12.opExtrude","SWEPT_FACE",FACE,{"disambiguationData":[OSD([sQuery(id+"F11.wireOp",EDGE,"E84.top")])]}),makeQuery(id+"F12.opExtrude","SWEPT_FACE",FACE,{"disambiguationData":[OSD([sQuery(id+"F11.wireOp",EDGE,"E85.top")])]}),makeQuery(id+"F12.opExtrude","SWEPT_FACE",FACE,{"disambiguationData":[OSD([sQuery(id+"F11.wireOp",EDGE,"E86.top")])]}),makeQuery(id+"F12.opExtrude","SWEPT_FACE",FACE,{"disambiguationData":[OSD([sQuery(id+"F11.wireOp",EDGE,"E87.top")])]}),makeQuery(id+"F12.opExtrude","SWEPT_FACE",FACE,{"disambiguationData":[OSD([sQuery(id+"F11.wireOp",EDGE,"E88.top")])]}),makeQuery(id+"F12.opExtrude","SWEPT_FACE",FACE,{"disambiguationData":[OSD([sQuery(id+"F11.wireOp",EDGE,"E89.top")])]}),makeQuery(id+"F12.opExtrude","SWEPT_FACE",FACE,{"disambiguationData":[OSD([sQuery(id+"F11.wireOp",EDGE,"E90.top")])]}),makeQuery(id+"F12.opExtrude","SWEPT_FACE",FACE,{"disambiguationData":[OSD([sQuery(id+"F11.wireOp",EDGE,"E91.top")])]}),makeQuery(id+"F12.opExtrude","SWEPT_FACE",FACE,{"disambiguationData":[OSD([sQuery(id+"F11.wireOp",EDGE,"E92.top")])]}),makeQuery(id+"F12.opExtrude","SWEPT_FACE",FACE,{"disambiguationData":[OSD([sQuery(id+"F11.wireOp",EDGE,"E93.top")])]}),makeQuery(id+"F12.opExtrude","SWEPT_FACE",FACE,{"disambiguationData":[OSD([sQuery(id+"F11.wireOp",EDGE,"E94.top")])]}),makeQuery(id+"F12.opExtrude","SWEPT_FACE",FACE,{"disambiguationData":[OSD([sQuery(id+"F11.wireOp",EDGE,"E95.top")])]}),makeQuery(id+"F12.opExtrude","SWEPT_FACE",FACE,{"disambiguationData":[OSD([sQuery(id+"F11.wireOp",EDGE,"E96.top")])]}),makeQuery(id+"F12.opExtrude","SWEPT_FACE",FACE,{"disambiguationData":[OSD([sQuery(id+"F11.wireOp",EDGE,"E97.top")])]}),makeQuery(id+"F12.opExtrude","SWEPT_FACE",FACE,{"disambiguationData":[OSD([sQuery(id+"F11.wireOp",EDGE,"E98.top")])]}),makeQuery(id+"F12.opExtrude","SWEPT_FACE",FACE,{"disambiguationData":[OSD([sQuery(id+"F11.wireOp",EDGE,"E99.top")])]}),makeQuery(id+"F12.opExtrude","SWEPT_FACE",FACE,{"disambiguationData":[OSD([sQuery(id+"F11.wireOp",EDGE,"E100.top")])]}),makeQuery(id+"F12.opExtrude","SWEPT_FACE",FACE,{"disambiguationData":[OSD([sQuery(id+"F11.wireOp",EDGE,"E101.top")])]})]}),makeQuery(id+"F14.opExtrude","SWEPT_FACE",FACE,{"disambiguationData":[OSD([sQuery(id+"F13.wireOp",EDGE,"E102.top")])]}),makeQuery(id+"F14.opExtrude","SWEPT_FACE",FACE,{"disambiguationData":[OSD([sQuery(id+"F13.wireOp",EDGE,"E103.top")])]}),makeQuery(id+"F14.opExtrude","SWEPT_FACE",FACE,{"disambiguationData":[OSD([sQuery(id+"F13.wireOp",EDGE,"E104.top")])]}),makeQuery(id+"F14.opExtrude","SWEPT_FACE",FACE,{"disambiguationData":[OSD([sQuery(id+"F13.wireOp",EDGE,"E105.top")])]}),makeQuery(id+"F14.opExtrude","SWEPT_FACE",FACE,{"disambiguationData":[OSD([sQuery(id+"F13.wireOp",EDGE,"E106.top")])]}),makeQuery(id+"F14.opExtrude","SWEPT_FACE",FACE,{"disambiguationData":[OSD([sQuery(id+"F13.wireOp",EDGE,"E107.top")])]}),makeQuery(id+"F14.opExtrude","SWEPT_FACE",FACE,{"disambiguationData":[OSD([sQuery(id+"F13.wireOp",EDGE,"E108.top")])]}),makeQuery(id+"F14.opExtrude","SWEPT_FACE",FACE,{"disambiguationData":[OSD([sQuery(id+"F13.wireOp",EDGE,"E109.top")])]}),makeQuery(id+"F14.opExtrude","SWEPT_FACE",FACE,{"disambiguationData":[OSD([sQuery(id+"F13.wireOp",EDGE,"E110.top")])]}),makeQuery(id+"F14.opExtrude","SWEPT_FACE",FACE,{"disambiguationData":[OSD([sQuery(id+"F13.wireOp",EDGE,"E111.top")])]}),makeQuery(id+"F14.opExtrude","SWEPT_FACE",FACE,{"disambiguationData":[OSD([sQuery(id+"F13.wireOp",EDGE,"E112.top")])]}),makeQuery(id+"F14.opExtrude","SWEPT_FACE",FACE,{"disambiguationData":[OSD([sQuery(id+"F13.wireOp",EDGE,"E113.top")])]}),makeQuery(id+"F14.opExtrude","SWEPT_FACE",FACE,{"disambiguationData":[OSD([sQuery(id+"F13.wireOp",EDGE,"E114.top")])]}),makeQuery(id+"F14.opExtrude","SWEPT_FACE",FACE,{"disambiguationData":[OSD([sQuery(id+"F13.wireOp",EDGE,"E115.top")])]}),makeQuery(id+"F14.opExtrude","SWEPT_FACE",FACE,{"disambiguationData":[OSD([sQuery(id+"F13.wireOp",EDGE,"E116.top")])]}),makeQuery(id+"F14.opExtrude","SWEPT_FACE",FACE,{"disambiguationData":[OSD([sQuery(id+"F13.wireOp",EDGE,"E117.top")])]}),makeQuery(id+"F14.opExtrude","SWEPT_FACE",FACE,{"disambiguationData":[OSD([sQuery(id+"F13.wireOp",EDGE,"E118.top")])]}),makeQuery(id+"F14.opExtrude","SWEPT_FACE",FACE,{"disambiguationData":[OSD([sQuery(id+"F13.wireOp",EDGE,"E119.top")])]}),makeQuery(id+"F14.opExtrude","SWEPT_FACE",FACE,{"disambiguationData":[OSD([sQuery(id+"F13.wireOp",EDGE,"E120.top")])]}),makeQuery(id+"F14.opExtrude","SWEPT_FACE",FACE,{"disambiguationData":[OSD([sQuery(id+"F13.wireOp",EDGE,"E121.top")])]}),makeQuery(id+"F14.opExtrude","SWEPT_FACE",FACE,{"disambiguationData":[OSD([sQuery(id+"F13.wireOp",EDGE,"E122.top")])]}),makeQuery(id+"F14.opExtrude","SWEPT_FACE",FACE,{"disambiguationData":[OSD([sQuery(id+"F13.wireOp",EDGE,"E123.top")])]}),makeQuery(id+"F14.opExtrude","SWEPT_FACE",FACE,{"disambiguationData":[OSD([sQuery(id+"F13.wireOp",EDGE,"E124.top")])]}),makeQuery(id+"F14.opExtrude","SWEPT_FACE",FACE,{"disambiguationData":[OSD([sQuery(id+"F13.wireOp",EDGE,"E125.top")])]}),makeQuery(id+"F14.opExtrude","SWEPT_FACE",FACE,{"disambiguationData":[OSD([sQuery(id+"F13.wireOp",EDGE,"E126.top")])]}),makeQuery(id+"F14.opExtrude","SWEPT_FACE",FACE,{"disambiguationData":[OSD([sQuery(id+"F13.wireOp",EDGE,"E127.top")])]}),makeQuery(id+"F14.opExtrude","SWEPT_FACE",FACE,{"disambiguationData":[OSD([sQuery(id+"F13.wireOp",EDGE,"E128.top")])]}),makeQuery(id+"F14.opExtrude","SWEPT_FACE",FACE,{"disambiguationData":[OSD([sQuery(id+"F13.wireOp",EDGE,"E129.top")])]}),makeQuery(id+"F14.opExtrude","SWEPT_FACE",FACE,{"disambiguationData":[OSD([sQuery(id+"F13.wireOp",EDGE,"E130.top")])]}),makeQuery(id+"F14.opExtrude","SWEPT_FACE",FACE,{"disambiguationData":[OSD([sQuery(id+"F13.wireOp",EDGE,"E131.top")])]}),makeQuery(id+"F14.opExtrude","SWEPT_FACE",FACE,{"disambiguationData":[OSD([sQuery(id+"F13.wireOp",EDGE,"E132.top")])]}),makeQuery(id+"F14.opExtrude","SWEPT_FACE",FACE,{"disambiguationData":[OSD([sQuery(id+"F13.wireOp",EDGE,"E133.top")])]})]});}
            var sketch = newSketch(context, id + "F15", { "sketchPlane" : qUnion([Q0])});
            skText(sketch, "E134", { "text": "To Tricia", "fontName": "OpenSans-Bold.ttf"});
            skText(sketch, "E135", { "text": "Love Brian", "fontName": "OpenSans-Regular.ttf"});
            const initialGuessF15  = {"E134": [-0.023, 0.01513, 1, 0, 0.00787], "E135": [-0.023, -0.023, 1, 0, 0.00675]};
            skSetInitialGuess(sketch, initialGuessF15);
            skSolve(sketch);
        }
        {
            var Q0;
            Q0 = qSketchRegion(id + "F15", true);
            extrude(context, id + "F16", {"entities" : qUnion([Q0]), "operationType" : NewBodyOperationType.REMOVE, "oppositeDirection" : true, "depth" : 1 * mm, "offsetDistance" : 25 * mm});
        }
        {
            var Q0;
            {var subQ0=sQuery(id+"F0.wireOp",EDGE,"E0.top");var subQ1=sQuery(id+"F4.wireOp",EDGE,"E3.top");Q0=makeQuery(id+"F8.boolean.opBoolean","SPLIT",FACE,{"disambiguationData":[TD([makeQuery(id+"F8.opExtrude","SWEPT_FACE",FACE,{"disambiguationData":[OSD([sQuery(id+"F7.wireOp",EDGE,"E5.bottom")])]})])],"derivedFrom":makeQuery(id+"F5.boolean.opBoolean","MERGE",FACE,{"derivedFrom":[makeQuery(id+"F1.opExtrude","SWEPT_FACE",FACE,{"disambiguationData":[OSD([subQ0])]}),makeQuery(id+"F5.opExtrude","SWEPT_FACE",FACE,{"disambiguationData":[OSD([subQ1])]})]})});}
            var sketch = newSketch(context, id + "F17", { "sketchPlane" : qUnion([Q0])});
            skLineSegment(sketch, "E136.bottom", {"start": v(-63, 103) * mm, "end": v(63, 103) * mm});
            skLineSegment(sketch, "E136.top", {"start": v(-63, 105) * mm, "end": v(63, 105) * mm});
            skLineSegment(sketch, "E136.left", {"start": v(-63, 103) * mm, "end": v(-63, 105) * mm});
            skLineSegment(sketch, "E136.right", {"start": v(63, 103) * mm, "end": v(63, 105) * mm});
            skLineSegment(sketch, "E137.bottom", {"start": v(-63, 35) * mm, "end": v(63, 35) * mm});
            skLineSegment(sketch, "E137.top", {"start": v(-63, 37) * mm, "end": v(63, 37) * mm});
            skLineSegment(sketch, "E137.left", {"start": v(-63, 35) * mm, "end": v(-63, 37) * mm});
            skLineSegment(sketch, "E137.right", {"start": v(63, 35) * mm, "end": v(63, 37) * mm});
            skLineSegment(sketch, "E138.bottom", {"start": v(-63, 69) * mm, "end": v(63, 69) * mm});
            skLineSegment(sketch, "E138.top", {"start": v(-63, 71) * mm, "end": v(63, 71) * mm});
            skLineSegment(sketch, "E138.left", {"start": v(-63, 69) * mm, "end": v(-63, 71) * mm});
            skLineSegment(sketch, "E138.right", {"start": v(63, 69) * mm, "end": v(63, 71) * mm});
            skSolve(sketch);
        }
        {
            var Q0;
            Q0 = qSketchRegion(id + "F17", true);
            extrude(context, id + "F18", {"entities" : qUnion([Q0]), "operationType" : NewBodyOperationType.ADD, "oppositeDirection" : true, "depth" : 3 * mm, "offsetDistance" : 25 * mm});
        }
        {
            var Q0;
            {var subQ0=sQuery(id+"F0.wireOp",EDGE,"E0.right");var subQ1=sQuery(id+"F4.wireOp",EDGE,"E3.right");Q0=makeQuery(id+"F10.boolean.opBoolean","SPLIT",FACE,{"disambiguationData":[TD([makeQuery(id+"F10.opExtrude","SWEPT_FACE",FACE,{"disambiguationData":[OSD([sQuery(id+"F9.wireOp",EDGE,"E37.bottom")])]})])],"derivedFrom":makeQuery(id+"F5.boolean.opBoolean","MERGE",FACE,{"derivedFrom":[makeQuery(id+"F1.opExtrude","SWEPT_FACE",FACE,{"disambiguationData":[OSD([subQ0])]}),makeQuery(id+"F5.opExtrude","SWEPT_FACE",FACE,{"disambiguationData":[OSD([subQ1])]})]})});}
            var sketch = newSketch(context, id + "F19", { "sketchPlane" : qUnion([Q0])});
            skLineSegment(sketch, "E139.bottom", {"start": v(-63, 105) * mm, "end": v(63, 105) * mm});
            skLineSegment(sketch, "E139.top", {"start": v(-63, 103) * mm, "end": v(63, 103) * mm});
            skLineSegment(sketch, "E139.left", {"start": v(-63, 105) * mm, "end": v(-63, 103) * mm});
            skLineSegment(sketch, "E139.right", {"start": v(63, 105) * mm, "end": v(63, 103) * mm});
            skLineSegment(sketch, "E140.bottom", {"start": v(-63, 71) * mm, "end": v(63, 71) * mm});
            skLineSegment(sketch, "E140.top", {"start": v(-63, 69) * mm, "end": v(63, 69) * mm});
            skLineSegment(sketch, "E140.left", {"start": v(-63, 71) * mm, "end": v(-63, 69) * mm});
            skLineSegment(sketch, "E140.right", {"start": v(63, 71) * mm, "end": v(63, 69) * mm});
            skLineSegment(sketch, "E141.bottom", {"start": v(-63, 37) * mm, "end": v(63, 37) * mm});
            skLineSegment(sketch, "E141.top", {"start": v(-63, 35) * mm, "end": v(63, 35) * mm});
            skLineSegment(sketch, "E141.left", {"start": v(-63, 37) * mm, "end": v(-63, 35) * mm});
            skLineSegment(sketch, "E141.right", {"start": v(63, 37) * mm, "end": v(63, 35) * mm});
            skSolve(sketch);
        }
        {
            var Q0;
            Q0 = qSketchRegion(id + "F19", true);
            extrude(context, id + "F20", {"entities" : qUnion([Q0]), "operationType" : NewBodyOperationType.ADD, "oppositeDirection" : true, "depth" : 3 * mm, "offsetDistance" : 25 * mm});
        }
        {
            var Q0;
            {var subQ0=sQuery(id+"F0.wireOp",EDGE,"E0.bottom");var subQ1=sQuery(id+"F4.wireOp",EDGE,"E3.bottom");Q0=makeQuery(id+"F12.boolean.opBoolean","SPLIT",FACE,{"disambiguationData":[TD([makeQuery(id+"F12.opExtrude","SWEPT_FACE",FACE,{"disambiguationData":[OSD([sQuery(id+"F11.wireOp",EDGE,"E70.bottom")])]})])],"derivedFrom":makeQuery(id+"F5.boolean.opBoolean","MERGE",FACE,{"derivedFrom":[makeQuery(id+"F1.opExtrude","SWEPT_FACE",FACE,{"disambiguationData":[OSD([subQ0])]}),makeQuery(id+"F5.opExtrude","SWEPT_FACE",FACE,{"disambiguationData":[OSD([subQ1])]})]})});}
            var sketch = newSketch(context, id + "F21", { "sketchPlane" : qUnion([Q0])});
            skLineSegment(sketch, "E142.bottom", {"start": v(-63, 71) * mm, "end": v(63, 71) * mm});
            skLineSegment(sketch, "E142.top", {"start": v(-63, 69) * mm, "end": v(63, 69) * mm});
            skLineSegment(sketch, "E142.left", {"start": v(-63, 71) * mm, "end": v(-63, 69) * mm});
            skLineSegment(sketch, "E142.right", {"start": v(63, 71) * mm, "end": v(63, 69) * mm});
            skLineSegment(sketch, "E143.bottom", {"start": v(-63, 105) * mm, "end": v(63, 105) * mm});
            skLineSegment(sketch, "E143.top", {"start": v(-63, 103) * mm, "end": v(63, 103) * mm});
            skLineSegment(sketch, "E143.left", {"start": v(-63, 105) * mm, "end": v(-63, 103) * mm});
            skLineSegment(sketch, "E143.right", {"start": v(63, 105) * mm, "end": v(63, 103) * mm});
            skLineSegment(sketch, "E144.bottom", {"start": v(-63, 37) * mm, "end": v(63, 37) * mm});
            skLineSegment(sketch, "E144.top", {"start": v(-63, 35) * mm, "end": v(63, 35) * mm});
            skLineSegment(sketch, "E144.left", {"start": v(-63, 37) * mm, "end": v(-63, 35) * mm});
            skLineSegment(sketch, "E144.right", {"start": v(63, 37) * mm, "end": v(63, 35) * mm});
            skSolve(sketch);
        }
        {
            var Q0;
            Q0 = qSketchRegion(id + "F21", true);
            extrude(context, id + "F22", {"entities" : qUnion([Q0]), "operationType" : NewBodyOperationType.ADD, "oppositeDirection" : true, "depth" : 3 * mm, "offsetDistance" : 25 * mm});
        }
        {
            var Q0;
            {var subQ0=sQuery(id+"F0.wireOp",EDGE,"E0.left");var subQ1=sQuery(id+"F4.wireOp",EDGE,"E3.left");Q0=makeQuery(id+"F14.boolean.opBoolean","SPLIT",FACE,{"disambiguationData":[TD([makeQuery(id+"F14.opExtrude","SWEPT_FACE",FACE,{"disambiguationData":[OSD([sQuery(id+"F13.wireOp",EDGE,"E104.right")])]})])],"derivedFrom":makeQuery(id+"F5.boolean.opBoolean","MERGE",FACE,{"derivedFrom":[makeQuery(id+"F1.opExtrude","SWEPT_FACE",FACE,{"disambiguationData":[OSD([subQ0])]}),makeQuery(id+"F5.opExtrude","SWEPT_FACE",FACE,{"disambiguationData":[OSD([subQ1])]})]})});}
            var sketch = newSketch(context, id + "F23", { "sketchPlane" : qUnion([Q0])});
            skLineSegment(sketch, "E145.bottom", {"start": v(-63, 37) * mm, "end": v(63, 37) * mm});
            skLineSegment(sketch, "E145.top", {"start": v(-63, 35) * mm, "end": v(63, 35) * mm});
            skLineSegment(sketch, "E145.left", {"start": v(-63, 37) * mm, "end": v(-63, 35) * mm});
            skLineSegment(sketch, "E145.right", {"start": v(63, 37) * mm, "end": v(63, 35) * mm});
            skLineSegment(sketch, "E146.bottom", {"start": v(-63, 71) * mm, "end": v(63, 71) * mm});
            skLineSegment(sketch, "E146.top", {"start": v(-63, 69) * mm, "end": v(63, 69) * mm});
            skLineSegment(sketch, "E146.left", {"start": v(-63, 71) * mm, "end": v(-63, 69) * mm});
            skLineSegment(sketch, "E146.right", {"start": v(63, 71) * mm, "end": v(63, 69) * mm});
            skLineSegment(sketch, "E147.bottom", {"start": v(-63, 105) * mm, "end": v(63, 105) * mm});
            skLineSegment(sketch, "E147.top", {"start": v(-63, 103) * mm, "end": v(63, 103) * mm});
            skLineSegment(sketch, "E147.left", {"start": v(-63, 105) * mm, "end": v(-63, 103) * mm});
            skLineSegment(sketch, "E147.right", {"start": v(63, 105) * mm, "end": v(63, 103) * mm});
            skSolve(sketch);
        }
        {
            var Q0;
            Q0 = qSketchRegion(id + "F23", true);
            extrude(context, id + "F24", {"entities" : qUnion([Q0]), "operationType" : NewBodyOperationType.ADD, "oppositeDirection" : true, "depth" : 3 * mm, "offsetDistance" : 25 * mm});
        }
        {
            var Q0;
            {var subQ46=sQuery(id+"F0.wireOp",EDGE,"E0.bottom");var subQ61=sQuery(id+"F4.wireOp",EDGE,"E3.bottom");var subQ102=makeQuery(id+"F5.boolean.opBoolean","MERGE",FACE,{"derivedFrom":[makeQuery(id+"F1.opExtrude","SWEPT_FACE",FACE,{"disambiguationData":[OSD([subQ46])]}),makeQuery(id+"F5.opExtrude","SWEPT_FACE",FACE,{"disambiguationData":[OSD([subQ61])]})]});Q0=makeQuery(id+"F22.boolean.opBoolean","MERGE",FACE,{"derivedFrom":[makeQuery(id+"F12.boolean.opBoolean","SPLIT",FACE,{"disambiguationData":[TD([makeQuery(id+"F12.opExtrude","SWEPT_FACE",FACE,{"disambiguationData":[OSD([sQuery(id+"F11.wireOp",EDGE,"E70.bottom")])]})])],"derivedFrom":subQ102}),makeQuery(id+"F12.boolean.opBoolean","SPLIT",FACE,{"disambiguationData":[TD([makeQuery(id+"F12.opExtrude","SWEPT_FACE",FACE,{"disambiguationData":[OSD([sQuery(id+"F11.wireOp",EDGE,"E71.right")])]})])],"derivedFrom":subQ102}),makeQuery(id+"F12.boolean.opBoolean","SPLIT",FACE,{"disambiguationData":[TD([makeQuery(id+"F12.opExtrude","SWEPT_FACE",FACE,{"disambiguationData":[OSD([sQuery(id+"F11.wireOp",EDGE,"E72.right")])]})])],"derivedFrom":subQ102}),makeQuery(id+"F12.boolean.opBoolean","SPLIT",FACE,{"disambiguationData":[TD([makeQuery(id+"F12.opExtrude","SWEPT_FACE",FACE,{"disambiguationData":[OSD([sQuery(id+"F11.wireOp",EDGE,"E73.right")])]})])],"derivedFrom":subQ102}),makeQuery(id+"F12.boolean.opBoolean","SPLIT",FACE,{"disambiguationData":[TD([makeQuery(id+"F12.opExtrude","SWEPT_FACE",FACE,{"disambiguationData":[OSD([sQuery(id+"F11.wireOp",EDGE,"E74.right")])]})])],"derivedFrom":subQ102}),makeQuery(id+"F12.boolean.opBoolean","SPLIT",FACE,{"disambiguationData":[TD([makeQuery(id+"F12.opExtrude","SWEPT_FACE",FACE,{"disambiguationData":[OSD([sQuery(id+"F11.wireOp",EDGE,"E75.right")])]})])],"derivedFrom":subQ102}),makeQuery(id+"F12.boolean.opBoolean","SPLIT",FACE,{"disambiguationData":[TD([makeQuery(id+"F12.opExtrude","SWEPT_FACE",FACE,{"disambiguationData":[OSD([sQuery(id+"F11.wireOp",EDGE,"E76.right")])]})])],"derivedFrom":subQ102}),makeQuery(id+"F12.boolean.opBoolean","SPLIT",FACE,{"disambiguationData":[TD([makeQuery(id+"F12.opExtrude","SWEPT_FACE",FACE,{"disambiguationData":[OSD([sQuery(id+"F11.wireOp",EDGE,"E77.right")])]})])],"derivedFrom":subQ102}),makeQuery(id+"F12.boolean.opBoolean","SPLIT",FACE,{"disambiguationData":[TD([makeQuery(id+"F12.opExtrude","SWEPT_FACE",FACE,{"disambiguationData":[OSD([sQuery(id+"F11.wireOp",EDGE,"E78.right")])]})])],"derivedFrom":subQ102}),makeQuery(id+"F12.boolean.opBoolean","SPLIT",FACE,{"disambiguationData":[TD([makeQuery(id+"F12.opExtrude","SWEPT_FACE",FACE,{"disambiguationData":[OSD([sQuery(id+"F11.wireOp",EDGE,"E79.right")])]})])],"derivedFrom":subQ102}),makeQuery(id+"F12.boolean.opBoolean","SPLIT",FACE,{"disambiguationData":[TD([makeQuery(id+"F12.opExtrude","SWEPT_FACE",FACE,{"disambiguationData":[OSD([sQuery(id+"F11.wireOp",EDGE,"E80.right")])]})])],"derivedFrom":subQ102}),makeQuery(id+"F12.boolean.opBoolean","SPLIT",FACE,{"disambiguationData":[TD([makeQuery(id+"F12.opExtrude","SWEPT_FACE",FACE,{"disambiguationData":[OSD([sQuery(id+"F11.wireOp",EDGE,"E81.right")])]})])],"derivedFrom":subQ102}),makeQuery(id+"F12.boolean.opBoolean","SPLIT",FACE,{"disambiguationData":[TD([makeQuery(id+"F12.opExtrude","SWEPT_FACE",FACE,{"disambiguationData":[OSD([sQuery(id+"F11.wireOp",EDGE,"E82.right")])]})])],"derivedFrom":subQ102}),makeQuery(id+"F12.boolean.opBoolean","SPLIT",FACE,{"disambiguationData":[TD([makeQuery(id+"F12.opExtrude","SWEPT_FACE",FACE,{"disambiguationData":[OSD([sQuery(id+"F11.wireOp",EDGE,"E83.right")])]})])],"derivedFrom":subQ102}),makeQuery(id+"F12.boolean.opBoolean","SPLIT",FACE,{"disambiguationData":[TD([makeQuery(id+"F12.opExtrude","SWEPT_FACE",FACE,{"disambiguationData":[OSD([sQuery(id+"F11.wireOp",EDGE,"E84.right")])]})])],"derivedFrom":subQ102}),makeQuery(id+"F12.boolean.opBoolean","SPLIT",FACE,{"disambiguationData":[TD([makeQuery(id+"F12.opExtrude","SWEPT_FACE",FACE,{"disambiguationData":[OSD([sQuery(id+"F11.wireOp",EDGE,"E85.left")])]})])],"derivedFrom":subQ102}),makeQuery(id+"F12.boolean.opBoolean","SPLIT",FACE,{"disambiguationData":[TD([makeQuery(id+"F12.opExtrude","SWEPT_FACE",FACE,{"disambiguationData":[OSD([sQuery(id+"F11.wireOp",EDGE,"E85.right")])]})])],"derivedFrom":subQ102}),makeQuery(id+"F12.boolean.opBoolean","SPLIT",FACE,{"disambiguationData":[TD([makeQuery(id+"F12.opExtrude","SWEPT_FACE",FACE,{"disambiguationData":[OSD([sQuery(id+"F11.wireOp",EDGE,"E87.right")])]})])],"derivedFrom":subQ102}),makeQuery(id+"F12.boolean.opBoolean","SPLIT",FACE,{"disambiguationData":[TD([makeQuery(id+"F12.opExtrude","SWEPT_FACE",FACE,{"disambiguationData":[OSD([sQuery(id+"F11.wireOp",EDGE,"E88.right")])]})])],"derivedFrom":subQ102}),makeQuery(id+"F12.boolean.opBoolean","SPLIT",FACE,{"disambiguationData":[TD([makeQuery(id+"F12.opExtrude","SWEPT_FACE",FACE,{"disambiguationData":[OSD([sQuery(id+"F11.wireOp",EDGE,"E89.right")])]})])],"derivedFrom":subQ102}),makeQuery(id+"F12.boolean.opBoolean","SPLIT",FACE,{"disambiguationData":[TD([makeQuery(id+"F12.opExtrude","SWEPT_FACE",FACE,{"disambiguationData":[OSD([sQuery(id+"F11.wireOp",EDGE,"E90.right")])]})])],"derivedFrom":subQ102}),makeQuery(id+"F12.boolean.opBoolean","SPLIT",FACE,{"disambiguationData":[TD([makeQuery(id+"F12.opExtrude","SWEPT_FACE",FACE,{"disambiguationData":[OSD([sQuery(id+"F11.wireOp",EDGE,"E91.right")])]})])],"derivedFrom":subQ102}),makeQuery(id+"F12.boolean.opBoolean","SPLIT",FACE,{"disambiguationData":[TD([makeQuery(id+"F12.opExtrude","SWEPT_FACE",FACE,{"disambiguationData":[OSD([sQuery(id+"F11.wireOp",EDGE,"E92.right")])]})])],"derivedFrom":subQ102}),makeQuery(id+"F12.boolean.opBoolean","SPLIT",FACE,{"disambiguationData":[TD([makeQuery(id+"F12.opExtrude","SWEPT_FACE",FACE,{"disambiguationData":[OSD([sQuery(id+"F11.wireOp",EDGE,"E93.right")])]})])],"derivedFrom":subQ102}),makeQuery(id+"F12.boolean.opBoolean","SPLIT",FACE,{"disambiguationData":[TD([makeQuery(id+"F12.opExtrude","SWEPT_FACE",FACE,{"disambiguationData":[OSD([sQuery(id+"F11.wireOp",EDGE,"E94.right")])]})])],"derivedFrom":subQ102}),makeQuery(id+"F12.boolean.opBoolean","SPLIT",FACE,{"disambiguationData":[TD([makeQuery(id+"F12.opExtrude","SWEPT_FACE",FACE,{"disambiguationData":[OSD([sQuery(id+"F11.wireOp",EDGE,"E95.right")])]})])],"derivedFrom":subQ102}),makeQuery(id+"F12.boolean.opBoolean","SPLIT",FACE,{"disambiguationData":[TD([makeQuery(id+"F12.opExtrude","SWEPT_FACE",FACE,{"disambiguationData":[OSD([sQuery(id+"F11.wireOp",EDGE,"E96.right")])]})])],"derivedFrom":subQ102}),makeQuery(id+"F12.boolean.opBoolean","SPLIT",FACE,{"disambiguationData":[TD([makeQuery(id+"F12.opExtrude","SWEPT_FACE",FACE,{"disambiguationData":[OSD([sQuery(id+"F11.wireOp",EDGE,"E97.right")])]})])],"derivedFrom":subQ102}),makeQuery(id+"F12.boolean.opBoolean","SPLIT",FACE,{"disambiguationData":[TD([makeQuery(id+"F12.opExtrude","SWEPT_FACE",FACE,{"disambiguationData":[OSD([sQuery(id+"F11.wireOp",EDGE,"E98.right")])]})])],"derivedFrom":subQ102}),makeQuery(id+"F12.boolean.opBoolean","SPLIT",FACE,{"disambiguationData":[TD([makeQuery(id+"F12.opExtrude","SWEPT_FACE",FACE,{"disambiguationData":[OSD([sQuery(id+"F11.wireOp",EDGE,"E99.right")])]})])],"derivedFrom":subQ102}),makeQuery(id+"F12.boolean.opBoolean","SPLIT",FACE,{"disambiguationData":[TD([makeQuery(id+"F12.opExtrude","SWEPT_FACE",FACE,{"disambiguationData":[OSD([sQuery(id+"F11.wireOp",EDGE,"E100.right")])]})])],"derivedFrom":subQ102}),makeQuery(id+"F22.opExtrude","CAP_FACE",FACE,{"disambiguationData":[OSD([sQuery(id+"F21.wireOp",EDGE,"E142.bottom"),sQuery(id+"F21.wireOp",EDGE,"E142.top"),sQuery(id+"F21.wireOp",EDGE,"E142.left"),sQuery(id+"F21.wireOp",EDGE,"E142.right")])],"isStart":true}),makeQuery(id+"F22.opExtrude","CAP_FACE",FACE,{"disambiguationData":[OSD([sQuery(id+"F21.wireOp",EDGE,"E143.bottom"),sQuery(id+"F21.wireOp",EDGE,"E143.top"),sQuery(id+"F21.wireOp",EDGE,"E143.left"),sQuery(id+"F21.wireOp",EDGE,"E143.right")])],"isStart":true}),makeQuery(id+"F22.opExtrude","CAP_FACE",FACE,{"disambiguationData":[OSD([sQuery(id+"F21.wireOp",EDGE,"E144.bottom"),sQuery(id+"F21.wireOp",EDGE,"E144.top"),sQuery(id+"F21.wireOp",EDGE,"E144.left"),sQuery(id+"F21.wireOp",EDGE,"E144.right")])],"isStart":true})]});}
            var sketch = newSketch(context, id + "F25", { "sketchPlane" : qUnion([Q0])});
            skText(sketch, "E148", { "text": "T", "fontName": "OpenSans-Bold.ttf"});
            const initialGuessF25  = {"E148": [-0.02152, 0.037, 1, 0, 0.066]};
            skSetInitialGuess(sketch, initialGuessF25);
            skSolve(sketch);
        }
        {
            var Q0;
            Q0 = qSketchRegion(id + "F25", true);
            extrude(context, id + "F26", {"entities" : qUnion([Q0]), "operationType" : NewBodyOperationType.ADD, "oppositeDirection" : true, "depth" : 3 * mm, "offsetDistance" : 25 * mm});
        }
        {
            var Q0;
            {var subQ64=sQuery(id+"F0.wireOp",EDGE,"E0.left");var subQ94=sQuery(id+"F4.wireOp",EDGE,"E3.left");var subQ134=makeQuery(id+"F5.boolean.opBoolean","MERGE",FACE,{"derivedFrom":[makeQuery(id+"F1.opExtrude","SWEPT_FACE",FACE,{"disambiguationData":[OSD([subQ64])]}),makeQuery(id+"F5.opExtrude","SWEPT_FACE",FACE,{"disambiguationData":[OSD([subQ94])]})]});Q0=makeQuery(id+"F24.boolean.opBoolean","MERGE",FACE,{"derivedFrom":[makeQuery(id+"F14.boolean.opBoolean","SPLIT",FACE,{"disambiguationData":[TD([makeQuery(id+"F14.opExtrude","SWEPT_FACE",FACE,{"disambiguationData":[OSD([sQuery(id+"F13.wireOp",EDGE,"E102.bottom")])]})])],"derivedFrom":subQ134}),makeQuery(id+"F14.boolean.opBoolean","SPLIT",FACE,{"disambiguationData":[TD([makeQuery(id+"F14.opExtrude","SWEPT_FACE",FACE,{"disambiguationData":[OSD([sQuery(id+"F13.wireOp",EDGE,"E103.right")])]})])],"derivedFrom":subQ134}),makeQuery(id+"F14.boolean.opBoolean","SPLIT",FACE,{"disambiguationData":[TD([makeQuery(id+"F14.opExtrude","SWEPT_FACE",FACE,{"disambiguationData":[OSD([sQuery(id+"F13.wireOp",EDGE,"E104.right")])]})])],"derivedFrom":subQ134}),makeQuery(id+"F14.boolean.opBoolean","SPLIT",FACE,{"disambiguationData":[TD([makeQuery(id+"F14.opExtrude","SWEPT_FACE",FACE,{"disambiguationData":[OSD([sQuery(id+"F13.wireOp",EDGE,"E105.right")])]})])],"derivedFrom":subQ134}),makeQuery(id+"F14.boolean.opBoolean","SPLIT",FACE,{"disambiguationData":[TD([makeQuery(id+"F14.opExtrude","SWEPT_FACE",FACE,{"disambiguationData":[OSD([sQuery(id+"F13.wireOp",EDGE,"E106.right")])]})])],"derivedFrom":subQ134}),makeQuery(id+"F14.boolean.opBoolean","SPLIT",FACE,{"disambiguationData":[TD([makeQuery(id+"F14.opExtrude","SWEPT_FACE",FACE,{"disambiguationData":[OSD([sQuery(id+"F13.wireOp",EDGE,"E107.right")])]})])],"derivedFrom":subQ134}),makeQuery(id+"F14.boolean.opBoolean","SPLIT",FACE,{"disambiguationData":[TD([makeQuery(id+"F14.opExtrude","SWEPT_FACE",FACE,{"disambiguationData":[OSD([sQuery(id+"F13.wireOp",EDGE,"E108.right")])]})])],"derivedFrom":subQ134}),makeQuery(id+"F14.boolean.opBoolean","SPLIT",FACE,{"disambiguationData":[TD([makeQuery(id+"F14.opExtrude","SWEPT_FACE",FACE,{"disambiguationData":[OSD([sQuery(id+"F13.wireOp",EDGE,"E109.right")])]})])],"derivedFrom":subQ134}),makeQuery(id+"F14.boolean.opBoolean","SPLIT",FACE,{"disambiguationData":[TD([makeQuery(id+"F14.opExtrude","SWEPT_FACE",FACE,{"disambiguationData":[OSD([sQuery(id+"F13.wireOp",EDGE,"E110.right")])]})])],"derivedFrom":subQ134}),makeQuery(id+"F14.boolean.opBoolean","SPLIT",FACE,{"disambiguationData":[TD([makeQuery(id+"F14.opExtrude","SWEPT_FACE",FACE,{"disambiguationData":[OSD([sQuery(id+"F13.wireOp",EDGE,"E111.right")])]})])],"derivedFrom":subQ134}),makeQuery(id+"F14.boolean.opBoolean","SPLIT",FACE,{"disambiguationData":[TD([makeQuery(id+"F14.opExtrude","SWEPT_FACE",FACE,{"disambiguationData":[OSD([sQuery(id+"F13.wireOp",EDGE,"E112.right")])]})])],"derivedFrom":subQ134}),makeQuery(id+"F14.boolean.opBoolean","SPLIT",FACE,{"disambiguationData":[TD([makeQuery(id+"F14.opExtrude","SWEPT_FACE",FACE,{"disambiguationData":[OSD([sQuery(id+"F13.wireOp",EDGE,"E113.right")])]})])],"derivedFrom":subQ134}),makeQuery(id+"F14.boolean.opBoolean","SPLIT",FACE,{"disambiguationData":[TD([makeQuery(id+"F14.opExtrude","SWEPT_FACE",FACE,{"disambiguationData":[OSD([sQuery(id+"F13.wireOp",EDGE,"E114.right")])]})])],"derivedFrom":subQ134}),makeQuery(id+"F14.boolean.opBoolean","SPLIT",FACE,{"disambiguationData":[TD([makeQuery(id+"F14.opExtrude","SWEPT_FACE",FACE,{"disambiguationData":[OSD([sQuery(id+"F13.wireOp",EDGE,"E115.right")])]})])],"derivedFrom":subQ134}),makeQuery(id+"F14.boolean.opBoolean","SPLIT",FACE,{"disambiguationData":[TD([makeQuery(id+"F14.opExtrude","SWEPT_FACE",FACE,{"disambiguationData":[OSD([sQuery(id+"F13.wireOp",EDGE,"E116.right")])]})])],"derivedFrom":subQ134}),makeQuery(id+"F14.boolean.opBoolean","SPLIT",FACE,{"disambiguationData":[TD([makeQuery(id+"F14.opExtrude","SWEPT_FACE",FACE,{"disambiguationData":[OSD([sQuery(id+"F13.wireOp",EDGE,"E117.right")])]})])],"derivedFrom":subQ134}),makeQuery(id+"F14.boolean.opBoolean","SPLIT",FACE,{"disambiguationData":[TD([makeQuery(id+"F14.opExtrude","SWEPT_FACE",FACE,{"disambiguationData":[OSD([sQuery(id+"F13.wireOp",EDGE,"E118.right")])]})])],"derivedFrom":subQ134}),makeQuery(id+"F14.boolean.opBoolean","SPLIT",FACE,{"disambiguationData":[TD([makeQuery(id+"F14.opExtrude","SWEPT_FACE",FACE,{"disambiguationData":[OSD([sQuery(id+"F13.wireOp",EDGE,"E119.right")])]})])],"derivedFrom":subQ134}),makeQuery(id+"F14.boolean.opBoolean","SPLIT",FACE,{"disambiguationData":[TD([makeQuery(id+"F14.opExtrude","SWEPT_FACE",FACE,{"disambiguationData":[OSD([sQuery(id+"F13.wireOp",EDGE,"E120.right")])]})])],"derivedFrom":subQ134}),makeQuery(id+"F14.boolean.opBoolean","SPLIT",FACE,{"disambiguationData":[TD([makeQuery(id+"F14.opExtrude","SWEPT_FACE",FACE,{"disambiguationData":[OSD([sQuery(id+"F13.wireOp",EDGE,"E121.right")])]})])],"derivedFrom":subQ134}),makeQuery(id+"F14.boolean.opBoolean","SPLIT",FACE,{"disambiguationData":[TD([makeQuery(id+"F14.opExtrude","SWEPT_FACE",FACE,{"disambiguationData":[OSD([sQuery(id+"F13.wireOp",EDGE,"E122.right")])]})])],"derivedFrom":subQ134}),makeQuery(id+"F14.boolean.opBoolean","SPLIT",FACE,{"disambiguationData":[TD([makeQuery(id+"F14.opExtrude","SWEPT_FACE",FACE,{"disambiguationData":[OSD([sQuery(id+"F13.wireOp",EDGE,"E123.right")])]})])],"derivedFrom":subQ134}),makeQuery(id+"F14.boolean.opBoolean","SPLIT",FACE,{"disambiguationData":[TD([makeQuery(id+"F14.opExtrude","SWEPT_FACE",FACE,{"disambiguationData":[OSD([sQuery(id+"F13.wireOp",EDGE,"E124.right")])]})])],"derivedFrom":subQ134}),makeQuery(id+"F14.boolean.opBoolean","SPLIT",FACE,{"disambiguationData":[TD([makeQuery(id+"F14.opExtrude","SWEPT_FACE",FACE,{"disambiguationData":[OSD([sQuery(id+"F13.wireOp",EDGE,"E125.right")])]})])],"derivedFrom":subQ134}),makeQuery(id+"F14.boolean.opBoolean","SPLIT",FACE,{"disambiguationData":[TD([makeQuery(id+"F14.opExtrude","SWEPT_FACE",FACE,{"disambiguationData":[OSD([sQuery(id+"F13.wireOp",EDGE,"E126.right")])]})])],"derivedFrom":subQ134}),makeQuery(id+"F14.boolean.opBoolean","SPLIT",FACE,{"disambiguationData":[TD([makeQuery(id+"F14.opExtrude","SWEPT_FACE",FACE,{"disambiguationData":[OSD([sQuery(id+"F13.wireOp",EDGE,"E127.right")])]})])],"derivedFrom":subQ134}),makeQuery(id+"F14.boolean.opBoolean","SPLIT",FACE,{"disambiguationData":[TD([makeQuery(id+"F14.opExtrude","SWEPT_FACE",FACE,{"disambiguationData":[OSD([sQuery(id+"F13.wireOp",EDGE,"E128.right")])]})])],"derivedFrom":subQ134}),makeQuery(id+"F14.boolean.opBoolean","SPLIT",FACE,{"disambiguationData":[TD([makeQuery(id+"F14.opExtrude","SWEPT_FACE",FACE,{"disambiguationData":[OSD([sQuery(id+"F13.wireOp",EDGE,"E129.right")])]})])],"derivedFrom":subQ134}),makeQuery(id+"F14.boolean.opBoolean","SPLIT",FACE,{"disambiguationData":[TD([makeQuery(id+"F14.opExtrude","SWEPT_FACE",FACE,{"disambiguationData":[OSD([sQuery(id+"F13.wireOp",EDGE,"E130.right")])]})])],"derivedFrom":subQ134}),makeQuery(id+"F14.boolean.opBoolean","SPLIT",FACE,{"disambiguationData":[TD([makeQuery(id+"F14.opExtrude","SWEPT_FACE",FACE,{"disambiguationData":[OSD([sQuery(id+"F13.wireOp",EDGE,"E131.right")])]})])],"derivedFrom":subQ134}),makeQuery(id+"F14.boolean.opBoolean","SPLIT",FACE,{"disambiguationData":[TD([makeQuery(id+"F14.opExtrude","SWEPT_FACE",FACE,{"disambiguationData":[OSD([sQuery(id+"F13.wireOp",EDGE,"E132.right")])]})])],"derivedFrom":subQ134}),makeQuery(id+"F24.opExtrude","CAP_FACE",FACE,{"disambiguationData":[OSD([sQuery(id+"F23.wireOp",EDGE,"E145.bottom"),sQuery(id+"F23.wireOp",EDGE,"E145.top"),sQuery(id+"F23.wireOp",EDGE,"E145.left"),sQuery(id+"F23.wireOp",EDGE,"E145.right")])],"isStart":true}),makeQuery(id+"F24.opExtrude","CAP_FACE",FACE,{"disambiguationData":[OSD([sQuery(id+"F23.wireOp",EDGE,"E146.bottom"),sQuery(id+"F23.wireOp",EDGE,"E146.top"),sQuery(id+"F23.wireOp",EDGE,"E146.left"),sQuery(id+"F23.wireOp",EDGE,"E146.right")])],"isStart":true}),makeQuery(id+"F24.opExtrude","CAP_FACE",FACE,{"disambiguationData":[OSD([sQuery(id+"F23.wireOp",EDGE,"E147.bottom"),sQuery(id+"F23.wireOp",EDGE,"E147.top"),sQuery(id+"F23.wireOp",EDGE,"E147.left"),sQuery(id+"F23.wireOp",EDGE,"E147.right")])],"isStart":true})]});}
            var sketch = newSketch(context, id + "F27", { "sketchPlane" : qUnion([Q0])});
            skText(sketch, "E149", { "text": "J", "fontName": "OpenSans-Bold.ttf"});
            const initialGuessF27  = {"E149": [-0.0137, 0.05116, 1, 0, 0.05184]};
            skSetInitialGuess(sketch, initialGuessF27);
            skSolve(sketch);
        }
        {
            var Q0;
            Q0 = qSketchRegion(id + "F27", true);
            extrude(context, id + "F28", {"entities" : qUnion([Q0]), "operationType" : NewBodyOperationType.ADD, "oppositeDirection" : true, "depth" : 3 * mm, "offsetDistance" : 25 * mm});
        }
        {
            var Q0;
            {var subQ11=sQuery(id+"F0.wireOp",EDGE,"E0.top");var subQ18=sQuery(id+"F4.wireOp",EDGE,"E3.top");var subQ38=makeQuery(id+"F5.boolean.opBoolean","MERGE",FACE,{"derivedFrom":[makeQuery(id+"F1.opExtrude","SWEPT_FACE",FACE,{"disambiguationData":[OSD([subQ11])]}),makeQuery(id+"F5.opExtrude","SWEPT_FACE",FACE,{"disambiguationData":[OSD([subQ18])]})]});Q0=makeQuery(id+"F18.boolean.opBoolean","MERGE",FACE,{"derivedFrom":[makeQuery(id+"F8.boolean.opBoolean","SPLIT",FACE,{"disambiguationData":[TD([makeQuery(id+"F8.opExtrude","SWEPT_FACE",FACE,{"disambiguationData":[OSD([sQuery(id+"F7.wireOp",EDGE,"E5.bottom")])]})])],"derivedFrom":subQ38}),makeQuery(id+"F8.boolean.opBoolean","SPLIT",FACE,{"disambiguationData":[TD([makeQuery(id+"F8.opExtrude","SWEPT_FACE",FACE,{"disambiguationData":[OSD([sQuery(id+"F7.wireOp",EDGE,"E6.right")])]})])],"derivedFrom":subQ38}),makeQuery(id+"F8.boolean.opBoolean","SPLIT",FACE,{"disambiguationData":[TD([makeQuery(id+"F8.opExtrude","SWEPT_FACE",FACE,{"disambiguationData":[OSD([sQuery(id+"F7.wireOp",EDGE,"E7.right")])]})])],"derivedFrom":subQ38}),makeQuery(id+"F8.boolean.opBoolean","SPLIT",FACE,{"disambiguationData":[TD([makeQuery(id+"F8.opExtrude","SWEPT_FACE",FACE,{"disambiguationData":[OSD([sQuery(id+"F7.wireOp",EDGE,"E8.right")])]})])],"derivedFrom":subQ38}),makeQuery(id+"F8.boolean.opBoolean","SPLIT",FACE,{"disambiguationData":[TD([makeQuery(id+"F8.opExtrude","SWEPT_FACE",FACE,{"disambiguationData":[OSD([sQuery(id+"F7.wireOp",EDGE,"E9.right")])]})])],"derivedFrom":subQ38}),makeQuery(id+"F8.boolean.opBoolean","SPLIT",FACE,{"disambiguationData":[TD([makeQuery(id+"F8.opExtrude","SWEPT_FACE",FACE,{"disambiguationData":[OSD([sQuery(id+"F7.wireOp",EDGE,"E10.right")])]})])],"derivedFrom":subQ38}),makeQuery(id+"F8.boolean.opBoolean","SPLIT",FACE,{"disambiguationData":[TD([makeQuery(id+"F8.opExtrude","SWEPT_FACE",FACE,{"disambiguationData":[OSD([sQuery(id+"F7.wireOp",EDGE,"E11.right")])]})])],"derivedFrom":subQ38}),makeQuery(id+"F8.boolean.opBoolean","SPLIT",FACE,{"disambiguationData":[TD([makeQuery(id+"F8.opExtrude","SWEPT_FACE",FACE,{"disambiguationData":[OSD([sQuery(id+"F7.wireOp",EDGE,"E12.right")])]})])],"derivedFrom":subQ38}),makeQuery(id+"F8.boolean.opBoolean","SPLIT",FACE,{"disambiguationData":[TD([makeQuery(id+"F8.opExtrude","SWEPT_FACE",FACE,{"disambiguationData":[OSD([sQuery(id+"F7.wireOp",EDGE,"E13.right")])]})])],"derivedFrom":subQ38}),makeQuery(id+"F8.boolean.opBoolean","SPLIT",FACE,{"disambiguationData":[TD([makeQuery(id+"F8.opExtrude","SWEPT_FACE",FACE,{"disambiguationData":[OSD([sQuery(id+"F7.wireOp",EDGE,"E14.right")])]})])],"derivedFrom":subQ38}),makeQuery(id+"F8.boolean.opBoolean","SPLIT",FACE,{"disambiguationData":[TD([makeQuery(id+"F8.opExtrude","SWEPT_FACE",FACE,{"disambiguationData":[OSD([sQuery(id+"F7.wireOp",EDGE,"E15.right")])]})])],"derivedFrom":subQ38}),makeQuery(id+"F8.boolean.opBoolean","SPLIT",FACE,{"disambiguationData":[TD([makeQuery(id+"F8.opExtrude","SWEPT_FACE",FACE,{"disambiguationData":[OSD([sQuery(id+"F7.wireOp",EDGE,"E16.right")])]})])],"derivedFrom":subQ38}),makeQuery(id+"F8.boolean.opBoolean","SPLIT",FACE,{"disambiguationData":[TD([makeQuery(id+"F8.opExtrude","SWEPT_FACE",FACE,{"disambiguationData":[OSD([sQuery(id+"F7.wireOp",EDGE,"E17.right")])]})])],"derivedFrom":subQ38}),makeQuery(id+"F8.boolean.opBoolean","SPLIT",FACE,{"disambiguationData":[TD([makeQuery(id+"F8.opExtrude","SWEPT_FACE",FACE,{"disambiguationData":[OSD([sQuery(id+"F7.wireOp",EDGE,"E18.right")])]})])],"derivedFrom":subQ38}),makeQuery(id+"F8.boolean.opBoolean","SPLIT",FACE,{"disambiguationData":[TD([makeQuery(id+"F8.opExtrude","SWEPT_FACE",FACE,{"disambiguationData":[OSD([sQuery(id+"F7.wireOp",EDGE,"E19.right")])]})])],"derivedFrom":subQ38}),makeQuery(id+"F8.boolean.opBoolean","SPLIT",FACE,{"disambiguationData":[TD([makeQuery(id+"F8.opExtrude","SWEPT_FACE",FACE,{"disambiguationData":[OSD([sQuery(id+"F7.wireOp",EDGE,"E20.right")])]})])],"derivedFrom":subQ38}),makeQuery(id+"F8.boolean.opBoolean","SPLIT",FACE,{"disambiguationData":[TD([makeQuery(id+"F8.opExtrude","SWEPT_FACE",FACE,{"disambiguationData":[OSD([sQuery(id+"F7.wireOp",EDGE,"E21.right")])]})])],"derivedFrom":subQ38}),makeQuery(id+"F8.boolean.opBoolean","SPLIT",FACE,{"disambiguationData":[TD([makeQuery(id+"F8.opExtrude","SWEPT_FACE",FACE,{"disambiguationData":[OSD([sQuery(id+"F7.wireOp",EDGE,"E22.right")])]})])],"derivedFrom":subQ38}),makeQuery(id+"F8.boolean.opBoolean","SPLIT",FACE,{"disambiguationData":[TD([makeQuery(id+"F8.opExtrude","SWEPT_FACE",FACE,{"disambiguationData":[OSD([sQuery(id+"F7.wireOp",EDGE,"E23.right")])]})])],"derivedFrom":subQ38}),makeQuery(id+"F8.boolean.opBoolean","SPLIT",FACE,{"disambiguationData":[TD([makeQuery(id+"F8.opExtrude","SWEPT_FACE",FACE,{"disambiguationData":[OSD([sQuery(id+"F7.wireOp",EDGE,"E24.right")])]})])],"derivedFrom":subQ38}),makeQuery(id+"F8.boolean.opBoolean","SPLIT",FACE,{"disambiguationData":[TD([makeQuery(id+"F8.opExtrude","SWEPT_FACE",FACE,{"disambiguationData":[OSD([sQuery(id+"F7.wireOp",EDGE,"E25.right")])]})])],"derivedFrom":subQ38}),makeQuery(id+"F8.boolean.opBoolean","SPLIT",FACE,{"disambiguationData":[TD([makeQuery(id+"F8.opExtrude","SWEPT_FACE",FACE,{"disambiguationData":[OSD([sQuery(id+"F7.wireOp",EDGE,"E26.right")])]})])],"derivedFrom":subQ38}),makeQuery(id+"F8.boolean.opBoolean","SPLIT",FACE,{"disambiguationData":[TD([makeQuery(id+"F8.opExtrude","SWEPT_FACE",FACE,{"disambiguationData":[OSD([sQuery(id+"F7.wireOp",EDGE,"E27.right")])]})])],"derivedFrom":subQ38}),makeQuery(id+"F8.boolean.opBoolean","SPLIT",FACE,{"disambiguationData":[TD([makeQuery(id+"F8.opExtrude","SWEPT_FACE",FACE,{"disambiguationData":[OSD([sQuery(id+"F7.wireOp",EDGE,"E28.right")])]})])],"derivedFrom":subQ38}),makeQuery(id+"F8.boolean.opBoolean","SPLIT",FACE,{"disambiguationData":[TD([makeQuery(id+"F8.opExtrude","SWEPT_FACE",FACE,{"disambiguationData":[OSD([sQuery(id+"F7.wireOp",EDGE,"E29.right")])]})])],"derivedFrom":subQ38}),makeQuery(id+"F8.boolean.opBoolean","SPLIT",FACE,{"disambiguationData":[TD([makeQuery(id+"F8.opExtrude","SWEPT_FACE",FACE,{"disambiguationData":[OSD([sQuery(id+"F7.wireOp",EDGE,"E30.right")])]})])],"derivedFrom":subQ38}),makeQuery(id+"F8.boolean.opBoolean","SPLIT",FACE,{"disambiguationData":[TD([makeQuery(id+"F8.opExtrude","SWEPT_FACE",FACE,{"disambiguationData":[OSD([sQuery(id+"F7.wireOp",EDGE,"E31.right")])]})])],"derivedFrom":subQ38}),makeQuery(id+"F8.boolean.opBoolean","SPLIT",FACE,{"disambiguationData":[TD([makeQuery(id+"F8.opExtrude","SWEPT_FACE",FACE,{"disambiguationData":[OSD([sQuery(id+"F7.wireOp",EDGE,"E32.right")])]})])],"derivedFrom":subQ38}),makeQuery(id+"F8.boolean.opBoolean","SPLIT",FACE,{"disambiguationData":[TD([makeQuery(id+"F8.opExtrude","SWEPT_FACE",FACE,{"disambiguationData":[OSD([sQuery(id+"F7.wireOp",EDGE,"E33.right")])]})])],"derivedFrom":subQ38}),makeQuery(id+"F8.boolean.opBoolean","SPLIT",FACE,{"disambiguationData":[TD([makeQuery(id+"F8.opExtrude","SWEPT_FACE",FACE,{"disambiguationData":[OSD([sQuery(id+"F7.wireOp",EDGE,"E34.right")])]})])],"derivedFrom":subQ38}),makeQuery(id+"F8.boolean.opBoolean","SPLIT",FACE,{"disambiguationData":[TD([makeQuery(id+"F8.opExtrude","SWEPT_FACE",FACE,{"disambiguationData":[OSD([sQuery(id+"F7.wireOp",EDGE,"E35.right")])]})])],"derivedFrom":subQ38}),makeQuery(id+"F18.opExtrude","CAP_FACE",FACE,{"disambiguationData":[OSD([sQuery(id+"F17.wireOp",EDGE,"E136.bottom"),sQuery(id+"F17.wireOp",EDGE,"E136.top"),sQuery(id+"F17.wireOp",EDGE,"E136.left"),sQuery(id+"F17.wireOp",EDGE,"E136.right")])],"isStart":true}),makeQuery(id+"F18.opExtrude","CAP_FACE",FACE,{"disambiguationData":[OSD([sQuery(id+"F17.wireOp",EDGE,"E137.bottom"),sQuery(id+"F17.wireOp",EDGE,"E137.top"),sQuery(id+"F17.wireOp",EDGE,"E137.left"),sQuery(id+"F17.wireOp",EDGE,"E137.right")])],"isStart":true}),makeQuery(id+"F18.opExtrude","CAP_FACE",FACE,{"disambiguationData":[OSD([sQuery(id+"F17.wireOp",EDGE,"E138.bottom"),sQuery(id+"F17.wireOp",EDGE,"E138.top"),sQuery(id+"F17.wireOp",EDGE,"E138.left"),sQuery(id+"F17.wireOp",EDGE,"E138.right")])],"isStart":true})]});}
            var sketch = newSketch(context, id + "F29", { "sketchPlane" : qUnion([Q0])});
            skText(sketch, "E150", { "text": "5", "fontName": "OpenSans-Bold.ttf"});
            const initialGuessF29  = {"E150": [-0.02355, 0.037, 1, 0, 0.066]};
            skSetInitialGuess(sketch, initialGuessF29);
            skSolve(sketch);
        }
        {
            var Q0;
            Q0 = qSketchRegion(id + "F29", true);
            extrude(context, id + "F30", {"entities" : qUnion([Q0]), "operationType" : NewBodyOperationType.ADD, "oppositeDirection" : true, "depth" : 3 * mm, "offsetDistance" : 25 * mm});
        }
        {
            var Q0;
            {var subQ5=sQuery(id+"F0.wireOp",EDGE,"E0.right");var subQ45=sQuery(id+"F4.wireOp",EDGE,"E3.right");var subQ70=makeQuery(id+"F5.boolean.opBoolean","MERGE",FACE,{"derivedFrom":[makeQuery(id+"F1.opExtrude","SWEPT_FACE",FACE,{"disambiguationData":[OSD([subQ5])]}),makeQuery(id+"F5.opExtrude","SWEPT_FACE",FACE,{"disambiguationData":[OSD([subQ45])]})]});Q0=makeQuery(id+"F20.boolean.opBoolean","MERGE",FACE,{"derivedFrom":[makeQuery(id+"F10.boolean.opBoolean","SPLIT",FACE,{"disambiguationData":[TD([makeQuery(id+"F10.opExtrude","SWEPT_FACE",FACE,{"disambiguationData":[OSD([sQuery(id+"F9.wireOp",EDGE,"E37.bottom")])]})])],"derivedFrom":subQ70}),makeQuery(id+"F10.boolean.opBoolean","SPLIT",FACE,{"disambiguationData":[TD([makeQuery(id+"F10.opExtrude","SWEPT_FACE",FACE,{"disambiguationData":[OSD([sQuery(id+"F9.wireOp",EDGE,"E38.right")])]})])],"derivedFrom":subQ70}),makeQuery(id+"F10.boolean.opBoolean","SPLIT",FACE,{"disambiguationData":[TD([makeQuery(id+"F10.opExtrude","SWEPT_FACE",FACE,{"disambiguationData":[OSD([sQuery(id+"F9.wireOp",EDGE,"E39.right")])]})])],"derivedFrom":subQ70}),makeQuery(id+"F10.boolean.opBoolean","SPLIT",FACE,{"disambiguationData":[TD([makeQuery(id+"F10.opExtrude","SWEPT_FACE",FACE,{"disambiguationData":[OSD([sQuery(id+"F9.wireOp",EDGE,"E40.right")])]})])],"derivedFrom":subQ70}),makeQuery(id+"F10.boolean.opBoolean","SPLIT",FACE,{"disambiguationData":[TD([makeQuery(id+"F10.opExtrude","SWEPT_FACE",FACE,{"disambiguationData":[OSD([sQuery(id+"F9.wireOp",EDGE,"E41.right")])]})])],"derivedFrom":subQ70}),makeQuery(id+"F10.boolean.opBoolean","SPLIT",FACE,{"disambiguationData":[TD([makeQuery(id+"F10.opExtrude","SWEPT_FACE",FACE,{"disambiguationData":[OSD([sQuery(id+"F9.wireOp",EDGE,"E42.right")])]})])],"derivedFrom":subQ70}),makeQuery(id+"F10.boolean.opBoolean","SPLIT",FACE,{"disambiguationData":[TD([makeQuery(id+"F10.opExtrude","SWEPT_FACE",FACE,{"disambiguationData":[OSD([sQuery(id+"F9.wireOp",EDGE,"E43.right")])]})])],"derivedFrom":subQ70}),makeQuery(id+"F10.boolean.opBoolean","SPLIT",FACE,{"disambiguationData":[TD([makeQuery(id+"F10.opExtrude","SWEPT_FACE",FACE,{"disambiguationData":[OSD([sQuery(id+"F9.wireOp",EDGE,"E44.right")])]})])],"derivedFrom":subQ70}),makeQuery(id+"F10.boolean.opBoolean","SPLIT",FACE,{"disambiguationData":[TD([makeQuery(id+"F10.opExtrude","SWEPT_FACE",FACE,{"disambiguationData":[OSD([sQuery(id+"F9.wireOp",EDGE,"E45.right")])]})])],"derivedFrom":subQ70}),makeQuery(id+"F10.boolean.opBoolean","SPLIT",FACE,{"disambiguationData":[TD([makeQuery(id+"F10.opExtrude","SWEPT_FACE",FACE,{"disambiguationData":[OSD([sQuery(id+"F9.wireOp",EDGE,"E46.right")])]})])],"derivedFrom":subQ70}),makeQuery(id+"F10.boolean.opBoolean","SPLIT",FACE,{"disambiguationData":[TD([makeQuery(id+"F10.opExtrude","SWEPT_FACE",FACE,{"disambiguationData":[OSD([sQuery(id+"F9.wireOp",EDGE,"E47.right")])]})])],"derivedFrom":subQ70}),makeQuery(id+"F10.boolean.opBoolean","SPLIT",FACE,{"disambiguationData":[TD([makeQuery(id+"F10.opExtrude","SWEPT_FACE",FACE,{"disambiguationData":[OSD([sQuery(id+"F9.wireOp",EDGE,"E48.right")])]})])],"derivedFrom":subQ70}),makeQuery(id+"F10.boolean.opBoolean","SPLIT",FACE,{"disambiguationData":[TD([makeQuery(id+"F10.opExtrude","SWEPT_FACE",FACE,{"disambiguationData":[OSD([sQuery(id+"F9.wireOp",EDGE,"E50.right")])]})])],"derivedFrom":subQ70}),makeQuery(id+"F10.boolean.opBoolean","SPLIT",FACE,{"disambiguationData":[TD([makeQuery(id+"F10.opExtrude","SWEPT_FACE",FACE,{"disambiguationData":[OSD([sQuery(id+"F9.wireOp",EDGE,"E51.right")])]})])],"derivedFrom":subQ70}),makeQuery(id+"F10.boolean.opBoolean","SPLIT",FACE,{"disambiguationData":[TD([makeQuery(id+"F10.opExtrude","SWEPT_FACE",FACE,{"disambiguationData":[OSD([sQuery(id+"F9.wireOp",EDGE,"E52.right")])]})])],"derivedFrom":subQ70}),makeQuery(id+"F10.boolean.opBoolean","SPLIT",FACE,{"disambiguationData":[TD([makeQuery(id+"F10.opExtrude","SWEPT_FACE",FACE,{"disambiguationData":[OSD([sQuery(id+"F9.wireOp",EDGE,"E53.right")])]})])],"derivedFrom":subQ70}),makeQuery(id+"F10.boolean.opBoolean","SPLIT",FACE,{"disambiguationData":[TD([makeQuery(id+"F10.opExtrude","SWEPT_FACE",FACE,{"disambiguationData":[OSD([sQuery(id+"F9.wireOp",EDGE,"E54.right")])]})])],"derivedFrom":subQ70}),makeQuery(id+"F10.boolean.opBoolean","SPLIT",FACE,{"disambiguationData":[TD([makeQuery(id+"F10.opExtrude","SWEPT_FACE",FACE,{"disambiguationData":[OSD([sQuery(id+"F9.wireOp",EDGE,"E55.right")])]})])],"derivedFrom":subQ70}),makeQuery(id+"F10.boolean.opBoolean","SPLIT",FACE,{"disambiguationData":[TD([makeQuery(id+"F10.opExtrude","SWEPT_FACE",FACE,{"disambiguationData":[OSD([sQuery(id+"F9.wireOp",EDGE,"E56.right")])]})])],"derivedFrom":subQ70}),makeQuery(id+"F10.boolean.opBoolean","SPLIT",FACE,{"disambiguationData":[TD([makeQuery(id+"F10.opExtrude","SWEPT_FACE",FACE,{"disambiguationData":[OSD([sQuery(id+"F9.wireOp",EDGE,"E57.right")])]})])],"derivedFrom":subQ70}),makeQuery(id+"F10.boolean.opBoolean","SPLIT",FACE,{"disambiguationData":[TD([makeQuery(id+"F10.opExtrude","SWEPT_FACE",FACE,{"disambiguationData":[OSD([sQuery(id+"F9.wireOp",EDGE,"E58.right")])]})])],"derivedFrom":subQ70}),makeQuery(id+"F10.boolean.opBoolean","SPLIT",FACE,{"disambiguationData":[TD([makeQuery(id+"F10.opExtrude","SWEPT_FACE",FACE,{"disambiguationData":[OSD([sQuery(id+"F9.wireOp",EDGE,"E59.right")])]})])],"derivedFrom":subQ70}),makeQuery(id+"F10.boolean.opBoolean","SPLIT",FACE,{"disambiguationData":[TD([makeQuery(id+"F10.opExtrude","SWEPT_FACE",FACE,{"disambiguationData":[OSD([sQuery(id+"F9.wireOp",EDGE,"E60.right")])]})])],"derivedFrom":subQ70}),makeQuery(id+"F10.boolean.opBoolean","SPLIT",FACE,{"disambiguationData":[TD([makeQuery(id+"F10.opExtrude","SWEPT_FACE",FACE,{"disambiguationData":[OSD([sQuery(id+"F9.wireOp",EDGE,"E61.right")])]})])],"derivedFrom":subQ70}),makeQuery(id+"F10.boolean.opBoolean","SPLIT",FACE,{"disambiguationData":[TD([makeQuery(id+"F10.opExtrude","SWEPT_FACE",FACE,{"disambiguationData":[OSD([sQuery(id+"F9.wireOp",EDGE,"E62.right")])]})])],"derivedFrom":subQ70}),makeQuery(id+"F10.boolean.opBoolean","SPLIT",FACE,{"disambiguationData":[TD([makeQuery(id+"F10.opExtrude","SWEPT_FACE",FACE,{"disambiguationData":[OSD([sQuery(id+"F9.wireOp",EDGE,"E63.right")])]})])],"derivedFrom":subQ70}),makeQuery(id+"F10.boolean.opBoolean","SPLIT",FACE,{"disambiguationData":[TD([makeQuery(id+"F10.opExtrude","SWEPT_FACE",FACE,{"disambiguationData":[OSD([sQuery(id+"F9.wireOp",EDGE,"E64.right")])]})])],"derivedFrom":subQ70}),makeQuery(id+"F10.boolean.opBoolean","SPLIT",FACE,{"disambiguationData":[TD([makeQuery(id+"F10.opExtrude","SWEPT_FACE",FACE,{"disambiguationData":[OSD([sQuery(id+"F9.wireOp",EDGE,"E65.right")])]})])],"derivedFrom":subQ70}),makeQuery(id+"F10.boolean.opBoolean","SPLIT",FACE,{"disambiguationData":[TD([makeQuery(id+"F10.opExtrude","SWEPT_FACE",FACE,{"disambiguationData":[OSD([sQuery(id+"F9.wireOp",EDGE,"E66.right")])]})])],"derivedFrom":subQ70}),makeQuery(id+"F10.boolean.opBoolean","SPLIT",FACE,{"disambiguationData":[TD([makeQuery(id+"F10.opExtrude","SWEPT_FACE",FACE,{"disambiguationData":[OSD([sQuery(id+"F9.wireOp",EDGE,"E67.right")])]})])],"derivedFrom":subQ70}),makeQuery(id+"F10.boolean.opBoolean","SPLIT",FACE,{"disambiguationData":[TD([makeQuery(id+"F10.opExtrude","SWEPT_FACE",FACE,{"disambiguationData":[OSD([sQuery(id+"F9.wireOp",EDGE,"E68.right")])]})])],"derivedFrom":subQ70}),makeQuery(id+"F20.opExtrude","CAP_FACE",FACE,{"disambiguationData":[OSD([sQuery(id+"F19.wireOp",EDGE,"E139.bottom"),sQuery(id+"F19.wireOp",EDGE,"E139.top"),sQuery(id+"F19.wireOp",EDGE,"E139.left"),sQuery(id+"F19.wireOp",EDGE,"E139.right")])],"isStart":true}),makeQuery(id+"F20.opExtrude","CAP_FACE",FACE,{"disambiguationData":[OSD([sQuery(id+"F19.wireOp",EDGE,"E140.bottom"),sQuery(id+"F19.wireOp",EDGE,"E140.top"),sQuery(id+"F19.wireOp",EDGE,"E140.left"),sQuery(id+"F19.wireOp",EDGE,"E140.right")])],"isStart":true}),makeQuery(id+"F20.opExtrude","CAP_FACE",FACE,{"disambiguationData":[OSD([sQuery(id+"F19.wireOp",EDGE,"E141.bottom"),sQuery(id+"F19.wireOp",EDGE,"E141.top"),sQuery(id+"F19.wireOp",EDGE,"E141.left"),sQuery(id+"F19.wireOp",EDGE,"E141.right")])],"isStart":true})]});}
            var sketch = newSketch(context, id + "F31", { "sketchPlane" : qUnion([Q0])});
            skText(sketch, "E151", { "text": "1", "fontName": "OpenSans-Bold.ttf"});
            const initialGuessF31  = {"E151": [-0.0241, 0.037, 1, 0, 0.066]};
            skSetInitialGuess(sketch, initialGuessF31);
            skSolve(sketch);
        }
        {
            var Q0;
            Q0 = qSketchRegion(id + "F31", true);
            extrude(context, id + "F32", {"entities" : qUnion([Q0]), "operationType" : NewBodyOperationType.ADD, "oppositeDirection" : true, "depth" : 3 * mm, "offsetDistance" : 25 * mm});
        }
    });
